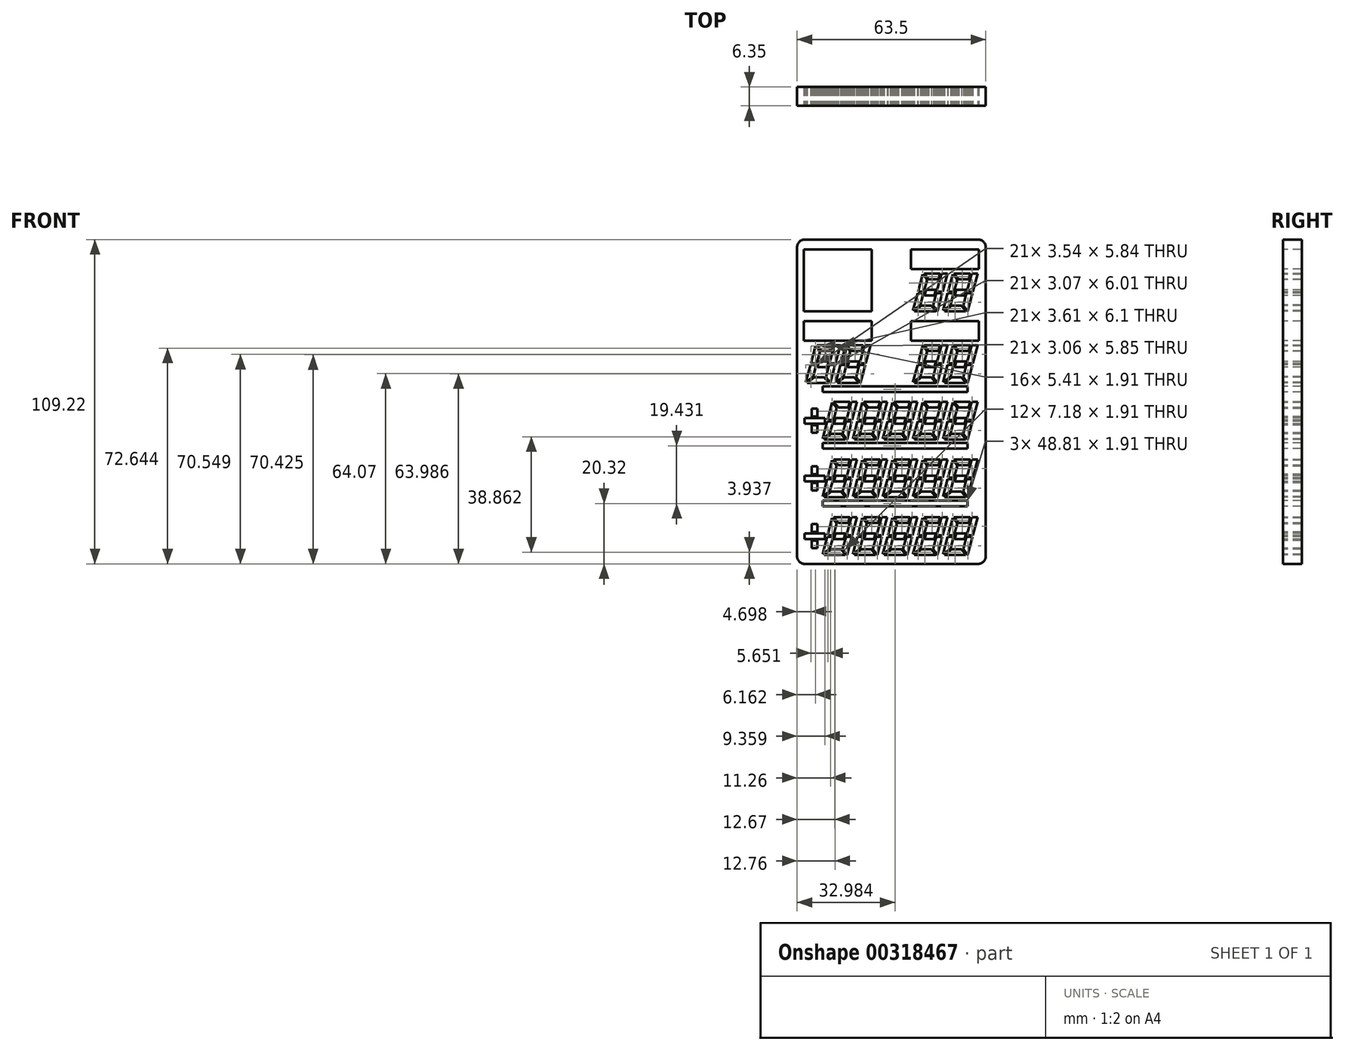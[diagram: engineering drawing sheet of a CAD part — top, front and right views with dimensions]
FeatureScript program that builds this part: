
annotation { "Feature Type Name" : "Feature", "Feature Type Description" : "" }
export const myFeature = defineFeature(function(context is Context, id is Id, definition is map)
    precondition{}
    {
        {
            var Q0;
            Q0=qCreatedBy(makeId("Front.planeOp"),FACE);
            var sketch = newSketch(context, id + "F0", { "sketchPlane" : qUnion([Q0])});
            skLineSegment(sketch, "E0.bottom", {"start": v(31.75, -54.61) * mm, "end": v(-31.75, -54.61) * mm});
            skLineSegment(sketch, "E0.top", {"start": v(31.75, 54.61) * mm, "end": v(-31.75, 54.6) * mm});
            skLineSegment(sketch, "E0.left", {"start": v(31.75, -54.61) * mm, "end": v(31.75, 54.61) * mm});
            skLineSegment(sketch, "E0.right", {"start": v(-31.75, -54.61) * mm, "end": v(-31.75, 54.6) * mm});
            skPoint(sketch, "E0.middle", {"position": v(0, 0) * mm});
            skSolve(sketch);
        }
        {
            var Q0;
            Q0 = qSketchRegion(id + "F0", true);
            extrude(context, id + "F1", {"entities" : qUnion([Q0]), "depth" : 6.35 * mm});
        }
        {
            var Q0;
            Q0=makeQuery(id+"F1.opExtrude","CAP_FACE",FACE,{"disambiguationData":[OSD([sQuery(id+"F0.wireOp",EDGE,"E0.bottom"),sQuery(id+"F0.wireOp",EDGE,"E0.top"),sQuery(id+"F0.wireOp",EDGE,"E0.left"),sQuery(id+"F0.wireOp",EDGE,"E0.right")])],"isStart":false});
            var sketch = newSketch(context, id + "F2", { "sketchPlane" : qUnion([Q0])});
            skLineSegment(sketch, "E1", {"start": v(21.11, -38.93) * mm, "end": v(26.52, -38.93) * mm});
            skLineSegment(sketch, "E2", {"start": v(26.52, -38.93) * mm, "end": v(26.01, -40.83) * mm});
            skLineSegment(sketch, "E3", {"start": v(26.01, -40.83) * mm, "end": v(22.7, -40.83) * mm});
            skLineSegment(sketch, "E4", {"start": v(22.7, -40.83) * mm, "end": v(21.11, -38.93) * mm});
            skLineSegment(sketch, "E5", {"start": v(27.05, -38.93) * mm, "end": v(29.02, -38.93) * mm});
            skLineSegment(sketch, "E6", {"start": v(29.02, -38.93) * mm, "end": v(27.39, -45.02) * mm});
            skLineSegment(sketch, "E7", {"start": v(27.05, -38.93) * mm, "end": v(25.41, -45.02) * mm});
            skLineSegment(sketch, "E8", {"start": v(25.41, -45.02) * mm, "end": v(27.39, -45.02) * mm});
            skLineSegment(sketch, "E9", {"start": v(25.28, -45.53) * mm, "end": v(27.25, -45.53) * mm});
            skLineSegment(sketch, "E10", {"start": v(27.25, -45.53) * mm, "end": v(25.64, -51.54) * mm});
            skLineSegment(sketch, "E11", {"start": v(20.65, -39.17) * mm, "end": v(22.15, -40.95) * mm});
            skLineSegment(sketch, "E12", {"start": v(22.15, -40.95) * mm, "end": v(21.06, -45.02) * mm});
            skLineSegment(sketch, "E13", {"start": v(21.06, -45.02) * mm, "end": v(19.09, -45.02) * mm});
            skLineSegment(sketch, "E14", {"start": v(19.09, -45.02) * mm, "end": v(20.65, -39.17) * mm});
            skLineSegment(sketch, "E15", {"start": v(25.28, -45.53) * mm, "end": v(24.18, -49.61) * mm});
            skLineSegment(sketch, "E16", {"start": v(24.18, -49.61) * mm, "end": v(25.64, -51.54) * mm});
            skLineSegment(sketch, "E17", {"start": v(25.06, -51.63) * mm, "end": v(23.63, -49.72) * mm});
            skLineSegment(sketch, "E18", {"start": v(23.63, -49.72) * mm, "end": v(20.33, -49.72) * mm});
            skLineSegment(sketch, "E19", {"start": v(25.06, -51.63) * mm, "end": v(17.89, -51.63) * mm});
            skLineSegment(sketch, "E20", {"start": v(17.89, -51.63) * mm, "end": v(20.33, -49.72) * mm});
            skLineSegment(sketch, "E21", {"start": v(20.92, -45.53) * mm, "end": v(18.95, -45.53) * mm});
            skLineSegment(sketch, "E22", {"start": v(18.95, -45.53) * mm, "end": v(17.39, -51.37) * mm});
            skLineSegment(sketch, "E23", {"start": v(17.39, -51.37) * mm, "end": v(19.88, -49.42) * mm});
            skLineSegment(sketch, "E24", {"start": v(19.88, -49.42) * mm, "end": v(20.92, -45.53) * mm});
            skLineSegment(sketch, "E25", {"start": v(21.77, -44.32) * mm, "end": v(21.26, -46.23) * mm});
            skLineSegment(sketch, "E26", {"start": v(21.26, -46.23) * mm, "end": v(24.56, -46.23) * mm});
            skLineSegment(sketch, "E27", {"start": v(24.56, -46.23) * mm, "end": v(25.08, -44.32) * mm});
            skLineSegment(sketch, "E28", {"start": v(25.08, -44.32) * mm, "end": v(21.77, -44.32) * mm});
            skLineSegment(sketch, "E29.0.1.0", {"start": v(21.26, -26.8) * mm, "end": v(24.56, -26.8) * mm});
            skLineSegment(sketch, "E29.0.1.1", {"start": v(18.95, -26.1) * mm, "end": v(17.39, -31.94) * mm});
            skLineSegment(sketch, "E29.0.1.2", {"start": v(22.15, -21.52) * mm, "end": v(21.06, -25.6) * mm});
            skLineSegment(sketch, "E29.0.1.3", {"start": v(29.02, -19.5) * mm, "end": v(27.39, -25.6) * mm});
            skLineSegment(sketch, "E29.0.1.4", {"start": v(26.01, -21.4) * mm, "end": v(22.7, -21.4) * mm});
            skLineSegment(sketch, "E29.0.1.5", {"start": v(25.06, -32.2) * mm, "end": v(17.89, -32.2) * mm});
            skLineSegment(sketch, "E29.0.1.6", {"start": v(27.05, -19.5) * mm, "end": v(25.41, -25.6) * mm});
            skLineSegment(sketch, "E29.0.1.7", {"start": v(23.63, -30.29) * mm, "end": v(20.33, -30.29) * mm});
            skLineSegment(sketch, "E29.0.1.8", {"start": v(25.08, -24.9) * mm, "end": v(21.77, -24.9) * mm});
            skLineSegment(sketch, "E29.0.1.9", {"start": v(25.28, -26.1) * mm, "end": v(24.18, -30.18) * mm});
            skLineSegment(sketch, "E29.0.1.10", {"start": v(27.25, -26.1) * mm, "end": v(25.64, -32.11) * mm});
            skLineSegment(sketch, "E29.0.1.11", {"start": v(19.09, -25.6) * mm, "end": v(20.65, -19.74) * mm});
            skLineSegment(sketch, "E29.0.1.12", {"start": v(21.11, -19.5) * mm, "end": v(26.52, -19.5) * mm});
            skLineSegment(sketch, "E29.0.1.13", {"start": v(20.65, -19.74) * mm, "end": v(22.15, -21.52) * mm});
            skLineSegment(sketch, "E29.0.1.14", {"start": v(21.06, -25.6) * mm, "end": v(19.09, -25.6) * mm});
            skLineSegment(sketch, "E29.0.1.15", {"start": v(19.88, -30) * mm, "end": v(20.92, -26.1) * mm});
            skLineSegment(sketch, "E29.0.1.16", {"start": v(22.7, -21.4) * mm, "end": v(21.11, -19.5) * mm});
            skLineSegment(sketch, "E29.0.1.17", {"start": v(17.89, -32.2) * mm, "end": v(20.33, -30.29) * mm});
            skLineSegment(sketch, "E29.0.1.18", {"start": v(27.05, -19.5) * mm, "end": v(29.02, -19.5) * mm});
            skLineSegment(sketch, "E29.0.1.19", {"start": v(20.92, -26.1) * mm, "end": v(18.95, -26.1) * mm});
            skLineSegment(sketch, "E29.0.1.20", {"start": v(17.39, -31.94) * mm, "end": v(19.88, -30) * mm});
            skLineSegment(sketch, "E29.0.1.21", {"start": v(25.06, -32.2) * mm, "end": v(23.63, -30.29) * mm});
            skLineSegment(sketch, "E29.0.1.22", {"start": v(26.52, -19.5) * mm, "end": v(26.01, -21.4) * mm});
            skLineSegment(sketch, "E29.0.1.23", {"start": v(24.18, -30.18) * mm, "end": v(25.64, -32.11) * mm});
            skLineSegment(sketch, "E29.0.1.24", {"start": v(21.77, -24.9) * mm, "end": v(21.26, -26.8) * mm});
            skLineSegment(sketch, "E29.0.1.25", {"start": v(25.28, -26.1) * mm, "end": v(27.25, -26.1) * mm});
            skLineSegment(sketch, "E29.0.1.26", {"start": v(25.41, -25.6) * mm, "end": v(27.39, -25.6) * mm});
            skLineSegment(sketch, "E29.0.1.27", {"start": v(24.56, -26.8) * mm, "end": v(25.08, -24.9) * mm});
            skLineSegment(sketch, "E29.0.2.0", {"start": v(21.26, -7.37) * mm, "end": v(24.56, -7.37) * mm});
            skLineSegment(sketch, "E29.0.2.1", {"start": v(18.95, -6.67) * mm, "end": v(17.39, -12.51) * mm});
            skLineSegment(sketch, "E29.0.2.2", {"start": v(22.15, -2.1) * mm, "end": v(21.06, -6.16) * mm});
            skLineSegment(sketch, "E29.0.2.3", {"start": v(29.02, -0.06) * mm, "end": v(27.39, -6.16) * mm});
            skLineSegment(sketch, "E29.0.2.4", {"start": v(26.01, -1.97) * mm, "end": v(22.7, -1.97) * mm});
            skLineSegment(sketch, "E29.0.2.5", {"start": v(25.06, -12.76) * mm, "end": v(17.89, -12.76) * mm});
            skLineSegment(sketch, "E29.0.2.6", {"start": v(27.05, -0.06) * mm, "end": v(25.41, -6.16) * mm});
            skLineSegment(sketch, "E29.0.2.7", {"start": v(23.63, -10.86) * mm, "end": v(20.33, -10.86) * mm});
            skLineSegment(sketch, "E29.0.2.8", {"start": v(25.08, -5.46) * mm, "end": v(21.77, -5.46) * mm});
            skLineSegment(sketch, "E29.0.2.9", {"start": v(25.28, -6.67) * mm, "end": v(24.18, -10.75) * mm});
            skLineSegment(sketch, "E29.0.2.10", {"start": v(27.25, -6.67) * mm, "end": v(25.64, -12.68) * mm});
            skLineSegment(sketch, "E29.0.2.11", {"start": v(19.09, -6.16) * mm, "end": v(20.65, -0.31) * mm});
            skLineSegment(sketch, "E29.0.2.12", {"start": v(21.11, -0.06) * mm, "end": v(26.52, -0.06) * mm});
            skLineSegment(sketch, "E29.0.2.13", {"start": v(20.65, -0.31) * mm, "end": v(22.15, -2.1) * mm});
            skLineSegment(sketch, "E29.0.2.14", {"start": v(21.06, -6.16) * mm, "end": v(19.09, -6.16) * mm});
            skLineSegment(sketch, "E29.0.2.15", {"start": v(19.88, -10.56) * mm, "end": v(20.92, -6.67) * mm});
            skLineSegment(sketch, "E29.0.2.16", {"start": v(22.7, -1.97) * mm, "end": v(21.11, -0.06) * mm});
            skLineSegment(sketch, "E29.0.2.17", {"start": v(17.89, -12.76) * mm, "end": v(20.33, -10.86) * mm});
            skLineSegment(sketch, "E29.0.2.18", {"start": v(27.05, -0.06) * mm, "end": v(29.02, -0.06) * mm});
            skLineSegment(sketch, "E29.0.2.19", {"start": v(20.92, -6.67) * mm, "end": v(18.95, -6.67) * mm});
            skLineSegment(sketch, "E29.0.2.20", {"start": v(17.39, -12.51) * mm, "end": v(19.88, -10.56) * mm});
            skLineSegment(sketch, "E29.0.2.21", {"start": v(25.06, -12.76) * mm, "end": v(23.63, -10.86) * mm});
            skLineSegment(sketch, "E29.0.2.22", {"start": v(26.52, -0.06) * mm, "end": v(26.01, -1.97) * mm});
            skLineSegment(sketch, "E29.0.2.23", {"start": v(24.18, -10.75) * mm, "end": v(25.64, -12.68) * mm});
            skLineSegment(sketch, "E29.0.2.24", {"start": v(21.77, -5.46) * mm, "end": v(21.26, -7.37) * mm});
            skLineSegment(sketch, "E29.0.2.25", {"start": v(25.28, -6.67) * mm, "end": v(27.25, -6.67) * mm});
            skLineSegment(sketch, "E29.0.2.26", {"start": v(25.41, -6.16) * mm, "end": v(27.39, -6.16) * mm});
            skLineSegment(sketch, "E29.0.2.27", {"start": v(24.56, -7.37) * mm, "end": v(25.08, -5.46) * mm});
            skLineSegment(sketch, "E29.1.0.0", {"start": v(11.12, -46.23) * mm, "end": v(14.43, -46.23) * mm});
            skLineSegment(sketch, "E29.1.0.1", {"start": v(8.81, -45.53) * mm, "end": v(7.25, -51.37) * mm});
            skLineSegment(sketch, "E29.1.0.2", {"start": v(12.01, -40.95) * mm, "end": v(10.92, -45.02) * mm});
            skLineSegment(sketch, "E29.1.0.3", {"start": v(18.88, -38.93) * mm, "end": v(17.25, -45.02) * mm});
            skLineSegment(sketch, "E29.1.0.4", {"start": v(15.87, -40.83) * mm, "end": v(12.57, -40.83) * mm});
            skLineSegment(sketch, "E29.1.0.5", {"start": v(14.93, -51.63) * mm, "end": v(7.75, -51.63) * mm});
            skLineSegment(sketch, "E29.1.0.6", {"start": v(16.9, -38.93) * mm, "end": v(15.27, -45.02) * mm});
            skLineSegment(sketch, "E29.1.0.7", {"start": v(13.49, -49.72) * mm, "end": v(10.19, -49.72) * mm});
            skLineSegment(sketch, "E29.1.0.8", {"start": v(14.94, -44.32) * mm, "end": v(11.63, -44.32) * mm});
            skLineSegment(sketch, "E29.1.0.9", {"start": v(15.14, -45.53) * mm, "end": v(14.04, -49.61) * mm});
            skLineSegment(sketch, "E29.1.0.10", {"start": v(17.11, -45.53) * mm, "end": v(15.5, -51.54) * mm});
            skLineSegment(sketch, "E29.1.0.11", {"start": v(8.95, -45.02) * mm, "end": v(10.52, -39.17) * mm});
            skLineSegment(sketch, "E29.1.0.12", {"start": v(10.97, -38.93) * mm, "end": v(16.38, -38.93) * mm});
            skLineSegment(sketch, "E29.1.0.13", {"start": v(10.52, -39.17) * mm, "end": v(12.01, -40.95) * mm});
            skLineSegment(sketch, "E29.1.0.14", {"start": v(10.92, -45.02) * mm, "end": v(8.95, -45.02) * mm});
            skLineSegment(sketch, "E29.1.0.15", {"start": v(9.74, -49.42) * mm, "end": v(10.78, -45.53) * mm});
            skLineSegment(sketch, "E29.1.0.16", {"start": v(12.57, -40.83) * mm, "end": v(10.97, -38.93) * mm});
            skLineSegment(sketch, "E29.1.0.17", {"start": v(7.75, -51.63) * mm, "end": v(10.19, -49.72) * mm});
            skLineSegment(sketch, "E29.1.0.18", {"start": v(16.9, -38.93) * mm, "end": v(18.88, -38.93) * mm});
            skLineSegment(sketch, "E29.1.0.19", {"start": v(10.78, -45.53) * mm, "end": v(8.81, -45.53) * mm});
            skLineSegment(sketch, "E29.1.0.20", {"start": v(7.25, -51.37) * mm, "end": v(9.74, -49.42) * mm});
            skLineSegment(sketch, "E29.1.0.21", {"start": v(14.93, -51.63) * mm, "end": v(13.49, -49.72) * mm});
            skLineSegment(sketch, "E29.1.0.22", {"start": v(16.38, -38.93) * mm, "end": v(15.87, -40.83) * mm});
            skLineSegment(sketch, "E29.1.0.23", {"start": v(14.04, -49.61) * mm, "end": v(15.5, -51.54) * mm});
            skLineSegment(sketch, "E29.1.0.24", {"start": v(11.63, -44.32) * mm, "end": v(11.12, -46.23) * mm});
            skLineSegment(sketch, "E29.1.0.25", {"start": v(15.14, -45.53) * mm, "end": v(17.11, -45.53) * mm});
            skLineSegment(sketch, "E29.1.0.26", {"start": v(15.27, -45.02) * mm, "end": v(17.25, -45.02) * mm});
            skLineSegment(sketch, "E29.1.0.27", {"start": v(14.43, -46.23) * mm, "end": v(14.94, -44.32) * mm});
            skLineSegment(sketch, "E29.1.1.0", {"start": v(11.12, -26.8) * mm, "end": v(14.43, -26.8) * mm});
            skLineSegment(sketch, "E29.1.1.1", {"start": v(8.81, -26.1) * mm, "end": v(7.25, -31.94) * mm});
            skLineSegment(sketch, "E29.1.1.2", {"start": v(12.01, -21.52) * mm, "end": v(10.92, -25.6) * mm});
            skLineSegment(sketch, "E29.1.1.3", {"start": v(18.88, -19.5) * mm, "end": v(17.25, -25.6) * mm});
            skLineSegment(sketch, "E29.1.1.4", {"start": v(15.87, -21.4) * mm, "end": v(12.57, -21.4) * mm});
            skLineSegment(sketch, "E29.1.1.5", {"start": v(14.93, -32.2) * mm, "end": v(7.75, -32.2) * mm});
            skLineSegment(sketch, "E29.1.1.6", {"start": v(16.9, -19.5) * mm, "end": v(15.27, -25.6) * mm});
            skLineSegment(sketch, "E29.1.1.7", {"start": v(13.49, -30.29) * mm, "end": v(10.19, -30.29) * mm});
            skLineSegment(sketch, "E29.1.1.8", {"start": v(14.94, -24.9) * mm, "end": v(11.63, -24.9) * mm});
            skLineSegment(sketch, "E29.1.1.9", {"start": v(15.14, -26.1) * mm, "end": v(14.04, -30.18) * mm});
            skLineSegment(sketch, "E29.1.1.10", {"start": v(17.11, -26.1) * mm, "end": v(15.5, -32.11) * mm});
            skLineSegment(sketch, "E29.1.1.11", {"start": v(8.95, -25.6) * mm, "end": v(10.52, -19.74) * mm});
            skLineSegment(sketch, "E29.1.1.12", {"start": v(10.97, -19.5) * mm, "end": v(16.38, -19.5) * mm});
            skLineSegment(sketch, "E29.1.1.13", {"start": v(10.52, -19.74) * mm, "end": v(12.01, -21.52) * mm});
            skLineSegment(sketch, "E29.1.1.14", {"start": v(10.92, -25.6) * mm, "end": v(8.95, -25.6) * mm});
            skLineSegment(sketch, "E29.1.1.15", {"start": v(9.74, -30) * mm, "end": v(10.78, -26.1) * mm});
            skLineSegment(sketch, "E29.1.1.16", {"start": v(12.57, -21.4) * mm, "end": v(10.97, -19.5) * mm});
            skLineSegment(sketch, "E29.1.1.17", {"start": v(7.75, -32.2) * mm, "end": v(10.19, -30.29) * mm});
            skLineSegment(sketch, "E29.1.1.18", {"start": v(16.9, -19.5) * mm, "end": v(18.88, -19.5) * mm});
            skLineSegment(sketch, "E29.1.1.19", {"start": v(10.78, -26.1) * mm, "end": v(8.81, -26.1) * mm});
            skLineSegment(sketch, "E29.1.1.20", {"start": v(7.25, -31.94) * mm, "end": v(9.74, -30) * mm});
            skLineSegment(sketch, "E29.1.1.21", {"start": v(14.93, -32.2) * mm, "end": v(13.49, -30.29) * mm});
            skLineSegment(sketch, "E29.1.1.22", {"start": v(16.38, -19.5) * mm, "end": v(15.87, -21.4) * mm});
            skLineSegment(sketch, "E29.1.1.23", {"start": v(14.04, -30.18) * mm, "end": v(15.5, -32.11) * mm});
            skLineSegment(sketch, "E29.1.1.24", {"start": v(11.63, -24.9) * mm, "end": v(11.12, -26.8) * mm});
            skLineSegment(sketch, "E29.1.1.25", {"start": v(15.14, -26.1) * mm, "end": v(17.11, -26.1) * mm});
            skLineSegment(sketch, "E29.1.1.26", {"start": v(15.27, -25.6) * mm, "end": v(17.25, -25.6) * mm});
            skLineSegment(sketch, "E29.1.1.27", {"start": v(14.43, -26.8) * mm, "end": v(14.94, -24.9) * mm});
            skLineSegment(sketch, "E29.1.2.0", {"start": v(11.12, -7.37) * mm, "end": v(14.43, -7.37) * mm});
            skLineSegment(sketch, "E29.1.2.1", {"start": v(8.81, -6.67) * mm, "end": v(7.25, -12.51) * mm});
            skLineSegment(sketch, "E29.1.2.2", {"start": v(12.01, -2.1) * mm, "end": v(10.92, -6.16) * mm});
            skLineSegment(sketch, "E29.1.2.3", {"start": v(18.88, -0.06) * mm, "end": v(17.25, -6.16) * mm});
            skLineSegment(sketch, "E29.1.2.4", {"start": v(15.87, -1.97) * mm, "end": v(12.57, -1.97) * mm});
            skLineSegment(sketch, "E29.1.2.5", {"start": v(14.93, -12.76) * mm, "end": v(7.75, -12.76) * mm});
            skLineSegment(sketch, "E29.1.2.6", {"start": v(16.9, -0.06) * mm, "end": v(15.27, -6.16) * mm});
            skLineSegment(sketch, "E29.1.2.7", {"start": v(13.49, -10.86) * mm, "end": v(10.19, -10.86) * mm});
            skLineSegment(sketch, "E29.1.2.8", {"start": v(14.94, -5.46) * mm, "end": v(11.63, -5.46) * mm});
            skLineSegment(sketch, "E29.1.2.9", {"start": v(15.14, -6.67) * mm, "end": v(14.04, -10.75) * mm});
            skLineSegment(sketch, "E29.1.2.10", {"start": v(17.11, -6.67) * mm, "end": v(15.5, -12.68) * mm});
            skLineSegment(sketch, "E29.1.2.11", {"start": v(8.95, -6.16) * mm, "end": v(10.52, -0.31) * mm});
            skLineSegment(sketch, "E29.1.2.12", {"start": v(10.97, -0.06) * mm, "end": v(16.38, -0.06) * mm});
            skLineSegment(sketch, "E29.1.2.13", {"start": v(10.52, -0.31) * mm, "end": v(12.01, -2.1) * mm});
            skLineSegment(sketch, "E29.1.2.14", {"start": v(10.92, -6.16) * mm, "end": v(8.95, -6.16) * mm});
            skLineSegment(sketch, "E29.1.2.15", {"start": v(9.74, -10.56) * mm, "end": v(10.78, -6.67) * mm});
            skLineSegment(sketch, "E29.1.2.16", {"start": v(12.57, -1.97) * mm, "end": v(10.97, -0.06) * mm});
            skLineSegment(sketch, "E29.1.2.17", {"start": v(7.75, -12.76) * mm, "end": v(10.19, -10.86) * mm});
            skLineSegment(sketch, "E29.1.2.18", {"start": v(16.9, -0.06) * mm, "end": v(18.88, -0.06) * mm});
            skLineSegment(sketch, "E29.1.2.19", {"start": v(10.78, -6.67) * mm, "end": v(8.81, -6.67) * mm});
            skLineSegment(sketch, "E29.1.2.20", {"start": v(7.25, -12.51) * mm, "end": v(9.74, -10.56) * mm});
            skLineSegment(sketch, "E29.1.2.21", {"start": v(14.93, -12.76) * mm, "end": v(13.49, -10.86) * mm});
            skLineSegment(sketch, "E29.1.2.22", {"start": v(16.38, -0.06) * mm, "end": v(15.87, -1.97) * mm});
            skLineSegment(sketch, "E29.1.2.23", {"start": v(14.04, -10.75) * mm, "end": v(15.5, -12.68) * mm});
            skLineSegment(sketch, "E29.1.2.24", {"start": v(11.63, -5.46) * mm, "end": v(11.12, -7.37) * mm});
            skLineSegment(sketch, "E29.1.2.25", {"start": v(15.14, -6.67) * mm, "end": v(17.11, -6.67) * mm});
            skLineSegment(sketch, "E29.1.2.26", {"start": v(15.27, -6.16) * mm, "end": v(17.25, -6.16) * mm});
            skLineSegment(sketch, "E29.1.2.27", {"start": v(14.43, -7.37) * mm, "end": v(14.94, -5.46) * mm});
            skLineSegment(sketch, "E29.2.0.0", {"start": v(0.98, -46.23) * mm, "end": v(4.29, -46.23) * mm});
            skLineSegment(sketch, "E29.2.0.1", {"start": v(-1.33, -45.53) * mm, "end": v(-2.9, -51.37) * mm});
            skLineSegment(sketch, "E29.2.0.2", {"start": v(1.87, -40.95) * mm, "end": v(0.78, -45.02) * mm});
            skLineSegment(sketch, "E29.2.0.3", {"start": v(8.74, -38.93) * mm, "end": v(7.1, -45.02) * mm});
            skLineSegment(sketch, "E29.2.0.4", {"start": v(5.73, -40.83) * mm, "end": v(2.43, -40.83) * mm});
            skLineSegment(sketch, "E29.2.0.5", {"start": v(4.79, -51.63) * mm, "end": v(-2.39, -51.63) * mm});
            skLineSegment(sketch, "E29.2.0.6", {"start": v(6.77, -38.93) * mm, "end": v(5.14, -45.02) * mm});
            skLineSegment(sketch, "E29.2.0.7", {"start": v(3.35, -49.72) * mm, "end": v(0.05, -49.72) * mm});
            skLineSegment(sketch, "E29.2.0.8", {"start": v(4.8, -44.32) * mm, "end": v(1.5, -44.32) * mm});
            skLineSegment(sketch, "E29.2.0.9", {"start": v(5, -45.53) * mm, "end": v(3.9, -49.61) * mm});
            skLineSegment(sketch, "E29.2.0.10", {"start": v(6.97, -45.53) * mm, "end": v(5.36, -51.54) * mm});
            skLineSegment(sketch, "E29.2.0.11", {"start": v(-1.2, -45.02) * mm, "end": v(0.38, -39.17) * mm});
            skLineSegment(sketch, "E29.2.0.12", {"start": v(0.83, -38.93) * mm, "end": v(6.24, -38.93) * mm});
            skLineSegment(sketch, "E29.2.0.13", {"start": v(0.38, -39.17) * mm, "end": v(1.87, -40.95) * mm});
            skLineSegment(sketch, "E29.2.0.14", {"start": v(0.78, -45.02) * mm, "end": v(-1.2, -45.02) * mm});
            skLineSegment(sketch, "E29.2.0.15", {"start": v(-0.4, -49.42) * mm, "end": v(0.65, -45.53) * mm});
            skLineSegment(sketch, "E29.2.0.16", {"start": v(2.43, -40.83) * mm, "end": v(0.83, -38.93) * mm});
            skLineSegment(sketch, "E29.2.0.17", {"start": v(-2.39, -51.63) * mm, "end": v(0.05, -49.72) * mm});
            skLineSegment(sketch, "E29.2.0.18", {"start": v(6.77, -38.93) * mm, "end": v(8.74, -38.93) * mm});
            skLineSegment(sketch, "E29.2.0.19", {"start": v(0.65, -45.53) * mm, "end": v(-1.33, -45.53) * mm});
            skLineSegment(sketch, "E29.2.0.20", {"start": v(-2.9, -51.37) * mm, "end": v(-0.4, -49.42) * mm});
            skLineSegment(sketch, "E29.2.0.21", {"start": v(4.79, -51.63) * mm, "end": v(3.35, -49.72) * mm});
            skLineSegment(sketch, "E29.2.0.22", {"start": v(6.24, -38.93) * mm, "end": v(5.73, -40.83) * mm});
            skLineSegment(sketch, "E29.2.0.23", {"start": v(3.9, -49.61) * mm, "end": v(5.36, -51.54) * mm});
            skLineSegment(sketch, "E29.2.0.24", {"start": v(1.5, -44.32) * mm, "end": v(0.98, -46.23) * mm});
            skLineSegment(sketch, "E29.2.0.25", {"start": v(5, -45.53) * mm, "end": v(6.97, -45.53) * mm});
            skLineSegment(sketch, "E29.2.0.26", {"start": v(5.14, -45.02) * mm, "end": v(7.1, -45.02) * mm});
            skLineSegment(sketch, "E29.2.0.27", {"start": v(4.29, -46.23) * mm, "end": v(4.8, -44.32) * mm});
            skLineSegment(sketch, "E29.2.1.0", {"start": v(0.98, -26.8) * mm, "end": v(4.29, -26.8) * mm});
            skLineSegment(sketch, "E29.2.1.1", {"start": v(-1.33, -26.1) * mm, "end": v(-2.9, -31.94) * mm});
            skLineSegment(sketch, "E29.2.1.2", {"start": v(1.87, -21.52) * mm, "end": v(0.78, -25.6) * mm});
            skLineSegment(sketch, "E29.2.1.3", {"start": v(8.74, -19.5) * mm, "end": v(7.1, -25.6) * mm});
            skLineSegment(sketch, "E29.2.1.4", {"start": v(5.73, -21.4) * mm, "end": v(2.43, -21.4) * mm});
            skLineSegment(sketch, "E29.2.1.5", {"start": v(4.79, -32.2) * mm, "end": v(-2.39, -32.2) * mm});
            skLineSegment(sketch, "E29.2.1.6", {"start": v(6.77, -19.5) * mm, "end": v(5.14, -25.6) * mm});
            skLineSegment(sketch, "E29.2.1.7", {"start": v(3.35, -30.29) * mm, "end": v(0.05, -30.29) * mm});
            skLineSegment(sketch, "E29.2.1.8", {"start": v(4.8, -24.9) * mm, "end": v(1.5, -24.9) * mm});
            skLineSegment(sketch, "E29.2.1.9", {"start": v(5, -26.1) * mm, "end": v(3.9, -30.18) * mm});
            skLineSegment(sketch, "E29.2.1.10", {"start": v(6.97, -26.1) * mm, "end": v(5.36, -32.11) * mm});
            skLineSegment(sketch, "E29.2.1.11", {"start": v(-1.2, -25.6) * mm, "end": v(0.38, -19.74) * mm});
            skLineSegment(sketch, "E29.2.1.12", {"start": v(0.83, -19.5) * mm, "end": v(6.24, -19.5) * mm});
            skLineSegment(sketch, "E29.2.1.13", {"start": v(0.38, -19.74) * mm, "end": v(1.87, -21.52) * mm});
            skLineSegment(sketch, "E29.2.1.14", {"start": v(0.78, -25.6) * mm, "end": v(-1.2, -25.6) * mm});
            skLineSegment(sketch, "E29.2.1.15", {"start": v(-0.4, -30) * mm, "end": v(0.65, -26.1) * mm});
            skLineSegment(sketch, "E29.2.1.16", {"start": v(2.43, -21.4) * mm, "end": v(0.83, -19.5) * mm});
            skLineSegment(sketch, "E29.2.1.17", {"start": v(-2.39, -32.2) * mm, "end": v(0.05, -30.29) * mm});
            skLineSegment(sketch, "E29.2.1.18", {"start": v(6.77, -19.5) * mm, "end": v(8.74, -19.5) * mm});
            skLineSegment(sketch, "E29.2.1.19", {"start": v(0.65, -26.1) * mm, "end": v(-1.33, -26.1) * mm});
            skLineSegment(sketch, "E29.2.1.20", {"start": v(-2.9, -31.94) * mm, "end": v(-0.4, -30) * mm});
            skLineSegment(sketch, "E29.2.1.21", {"start": v(4.79, -32.2) * mm, "end": v(3.35, -30.29) * mm});
            skLineSegment(sketch, "E29.2.1.22", {"start": v(6.24, -19.5) * mm, "end": v(5.73, -21.4) * mm});
            skLineSegment(sketch, "E29.2.1.23", {"start": v(3.9, -30.18) * mm, "end": v(5.36, -32.11) * mm});
            skLineSegment(sketch, "E29.2.1.24", {"start": v(1.5, -24.9) * mm, "end": v(0.98, -26.8) * mm});
            skLineSegment(sketch, "E29.2.1.25", {"start": v(5, -26.1) * mm, "end": v(6.97, -26.1) * mm});
            skLineSegment(sketch, "E29.2.1.26", {"start": v(5.14, -25.6) * mm, "end": v(7.1, -25.6) * mm});
            skLineSegment(sketch, "E29.2.1.27", {"start": v(4.29, -26.8) * mm, "end": v(4.8, -24.9) * mm});
            skLineSegment(sketch, "E29.2.2.0", {"start": v(0.98, -7.37) * mm, "end": v(4.29, -7.37) * mm});
            skLineSegment(sketch, "E29.2.2.1", {"start": v(-1.33, -6.67) * mm, "end": v(-2.9, -12.51) * mm});
            skLineSegment(sketch, "E29.2.2.2", {"start": v(1.87, -2.1) * mm, "end": v(0.78, -6.16) * mm});
            skLineSegment(sketch, "E29.2.2.3", {"start": v(8.74, -0.06) * mm, "end": v(7.1, -6.16) * mm});
            skLineSegment(sketch, "E29.2.2.4", {"start": v(5.73, -1.97) * mm, "end": v(2.43, -1.97) * mm});
            skLineSegment(sketch, "E29.2.2.5", {"start": v(4.79, -12.76) * mm, "end": v(-2.39, -12.76) * mm});
            skLineSegment(sketch, "E29.2.2.6", {"start": v(6.77, -0.06) * mm, "end": v(5.14, -6.16) * mm});
            skLineSegment(sketch, "E29.2.2.7", {"start": v(3.35, -10.86) * mm, "end": v(0.05, -10.86) * mm});
            skLineSegment(sketch, "E29.2.2.8", {"start": v(4.8, -5.46) * mm, "end": v(1.5, -5.46) * mm});
            skLineSegment(sketch, "E29.2.2.9", {"start": v(5, -6.67) * mm, "end": v(3.9, -10.75) * mm});
            skLineSegment(sketch, "E29.2.2.10", {"start": v(6.97, -6.67) * mm, "end": v(5.36, -12.68) * mm});
            skLineSegment(sketch, "E29.2.2.11", {"start": v(-1.2, -6.16) * mm, "end": v(0.38, -0.31) * mm});
            skLineSegment(sketch, "E29.2.2.12", {"start": v(0.83, -0.06) * mm, "end": v(6.24, -0.06) * mm});
            skLineSegment(sketch, "E29.2.2.13", {"start": v(0.38, -0.31) * mm, "end": v(1.87, -2.1) * mm});
            skLineSegment(sketch, "E29.2.2.14", {"start": v(0.78, -6.16) * mm, "end": v(-1.2, -6.16) * mm});
            skLineSegment(sketch, "E29.2.2.15", {"start": v(-0.4, -10.56) * mm, "end": v(0.65, -6.67) * mm});
            skLineSegment(sketch, "E29.2.2.16", {"start": v(2.43, -1.97) * mm, "end": v(0.83, -0.06) * mm});
            skLineSegment(sketch, "E29.2.2.17", {"start": v(-2.39, -12.76) * mm, "end": v(0.05, -10.86) * mm});
            skLineSegment(sketch, "E29.2.2.18", {"start": v(6.77, -0.06) * mm, "end": v(8.74, -0.06) * mm});
            skLineSegment(sketch, "E29.2.2.19", {"start": v(0.65, -6.67) * mm, "end": v(-1.33, -6.67) * mm});
            skLineSegment(sketch, "E29.2.2.20", {"start": v(-2.9, -12.51) * mm, "end": v(-0.4, -10.56) * mm});
            skLineSegment(sketch, "E29.2.2.21", {"start": v(4.79, -12.76) * mm, "end": v(3.35, -10.86) * mm});
            skLineSegment(sketch, "E29.2.2.22", {"start": v(6.24, -0.06) * mm, "end": v(5.73, -1.97) * mm});
            skLineSegment(sketch, "E29.2.2.23", {"start": v(3.9, -10.75) * mm, "end": v(5.36, -12.68) * mm});
            skLineSegment(sketch, "E29.2.2.24", {"start": v(1.5, -5.46) * mm, "end": v(0.98, -7.37) * mm});
            skLineSegment(sketch, "E29.2.2.25", {"start": v(5, -6.67) * mm, "end": v(6.97, -6.67) * mm});
            skLineSegment(sketch, "E29.2.2.26", {"start": v(5.14, -6.16) * mm, "end": v(7.1, -6.16) * mm});
            skLineSegment(sketch, "E29.2.2.27", {"start": v(4.29, -7.37) * mm, "end": v(4.8, -5.46) * mm});
            skLineSegment(sketch, "E29.3.0.0", {"start": v(-9.15, -46.23) * mm, "end": v(-5.85, -46.23) * mm});
            skLineSegment(sketch, "E29.3.0.1", {"start": v(-11.47, -45.53) * mm, "end": v(-13.03, -51.37) * mm});
            skLineSegment(sketch, "E29.3.0.2", {"start": v(-8.27, -40.95) * mm, "end": v(-9.36, -45.02) * mm});
            skLineSegment(sketch, "E29.3.0.3", {"start": v(-1.4, -38.93) * mm, "end": v(-3.03, -45.02) * mm});
            skLineSegment(sketch, "E29.3.0.4", {"start": v(-4.4, -40.83) * mm, "end": v(-7.7, -40.83) * mm});
            skLineSegment(sketch, "E29.3.0.5", {"start": v(-5.35, -51.63) * mm, "end": v(-12.53, -51.63) * mm});
            skLineSegment(sketch, "E29.3.0.6", {"start": v(-3.37, -38.93) * mm, "end": v(-5, -45.02) * mm});
            skLineSegment(sketch, "E29.3.0.7", {"start": v(-6.79, -49.72) * mm, "end": v(-10.1, -49.72) * mm});
            skLineSegment(sketch, "E29.3.0.8", {"start": v(-5.34, -44.32) * mm, "end": v(-8.64, -44.32) * mm});
            skLineSegment(sketch, "E29.3.0.9", {"start": v(-5.14, -45.53) * mm, "end": v(-6.23, -49.61) * mm});
            skLineSegment(sketch, "E29.3.0.10", {"start": v(-3.17, -45.53) * mm, "end": v(-4.78, -51.54) * mm});
            skLineSegment(sketch, "E29.3.0.11", {"start": v(-11.33, -45.02) * mm, "end": v(-9.76, -39.17) * mm});
            skLineSegment(sketch, "E29.3.0.12", {"start": v(-9.3, -38.93) * mm, "end": v(-3.9, -38.93) * mm});
            skLineSegment(sketch, "E29.3.0.13", {"start": v(-9.76, -39.17) * mm, "end": v(-8.27, -40.95) * mm});
            skLineSegment(sketch, "E29.3.0.14", {"start": v(-9.36, -45.02) * mm, "end": v(-11.33, -45.02) * mm});
            skLineSegment(sketch, "E29.3.0.15", {"start": v(-10.54, -49.42) * mm, "end": v(-9.5, -45.53) * mm});
            skLineSegment(sketch, "E29.3.0.16", {"start": v(-7.7, -40.83) * mm, "end": v(-9.3, -38.93) * mm});
            skLineSegment(sketch, "E29.3.0.17", {"start": v(-12.53, -51.63) * mm, "end": v(-10.1, -49.72) * mm});
            skLineSegment(sketch, "E29.3.0.18", {"start": v(-3.37, -38.93) * mm, "end": v(-1.4, -38.93) * mm});
            skLineSegment(sketch, "E29.3.0.19", {"start": v(-9.5, -45.53) * mm, "end": v(-11.47, -45.53) * mm});
            skLineSegment(sketch, "E29.3.0.20", {"start": v(-13.03, -51.37) * mm, "end": v(-10.54, -49.42) * mm});
            skLineSegment(sketch, "E29.3.0.21", {"start": v(-5.35, -51.63) * mm, "end": v(-6.79, -49.72) * mm});
            skLineSegment(sketch, "E29.3.0.22", {"start": v(-3.9, -38.93) * mm, "end": v(-4.4, -40.83) * mm});
            skLineSegment(sketch, "E29.3.0.23", {"start": v(-6.23, -49.61) * mm, "end": v(-4.78, -51.54) * mm});
            skLineSegment(sketch, "E29.3.0.24", {"start": v(-8.64, -44.32) * mm, "end": v(-9.15, -46.23) * mm});
            skLineSegment(sketch, "E29.3.0.25", {"start": v(-5.14, -45.53) * mm, "end": v(-3.17, -45.53) * mm});
            skLineSegment(sketch, "E29.3.0.26", {"start": v(-5, -45.02) * mm, "end": v(-3.03, -45.02) * mm});
            skLineSegment(sketch, "E29.3.0.27", {"start": v(-5.85, -46.23) * mm, "end": v(-5.34, -44.32) * mm});
            skLineSegment(sketch, "E29.3.1.0", {"start": v(-9.15, -26.8) * mm, "end": v(-5.85, -26.8) * mm});
            skLineSegment(sketch, "E29.3.1.1", {"start": v(-11.47, -26.1) * mm, "end": v(-13.03, -31.94) * mm});
            skLineSegment(sketch, "E29.3.1.2", {"start": v(-8.27, -21.52) * mm, "end": v(-9.36, -25.6) * mm});
            skLineSegment(sketch, "E29.3.1.3", {"start": v(-1.4, -19.5) * mm, "end": v(-3.03, -25.6) * mm});
            skLineSegment(sketch, "E29.3.1.4", {"start": v(-4.4, -21.4) * mm, "end": v(-7.7, -21.4) * mm});
            skLineSegment(sketch, "E29.3.1.5", {"start": v(-5.35, -32.2) * mm, "end": v(-12.53, -32.2) * mm});
            skLineSegment(sketch, "E29.3.1.6", {"start": v(-3.37, -19.5) * mm, "end": v(-5, -25.6) * mm});
            skLineSegment(sketch, "E29.3.1.7", {"start": v(-6.79, -30.29) * mm, "end": v(-10.1, -30.29) * mm});
            skLineSegment(sketch, "E29.3.1.8", {"start": v(-5.34, -24.9) * mm, "end": v(-8.64, -24.9) * mm});
            skLineSegment(sketch, "E29.3.1.9", {"start": v(-5.14, -26.1) * mm, "end": v(-6.23, -30.18) * mm});
            skLineSegment(sketch, "E29.3.1.10", {"start": v(-3.17, -26.1) * mm, "end": v(-4.78, -32.11) * mm});
            skLineSegment(sketch, "E29.3.1.11", {"start": v(-11.33, -25.6) * mm, "end": v(-9.76, -19.74) * mm});
            skLineSegment(sketch, "E29.3.1.12", {"start": v(-9.3, -19.5) * mm, "end": v(-3.9, -19.5) * mm});
            skLineSegment(sketch, "E29.3.1.13", {"start": v(-9.76, -19.74) * mm, "end": v(-8.27, -21.52) * mm});
            skLineSegment(sketch, "E29.3.1.14", {"start": v(-9.36, -25.6) * mm, "end": v(-11.33, -25.6) * mm});
            skLineSegment(sketch, "E29.3.1.15", {"start": v(-10.54, -30) * mm, "end": v(-9.5, -26.1) * mm});
            skLineSegment(sketch, "E29.3.1.16", {"start": v(-7.7, -21.4) * mm, "end": v(-9.3, -19.5) * mm});
            skLineSegment(sketch, "E29.3.1.17", {"start": v(-12.53, -32.2) * mm, "end": v(-10.1, -30.29) * mm});
            skLineSegment(sketch, "E29.3.1.18", {"start": v(-3.37, -19.5) * mm, "end": v(-1.4, -19.5) * mm});
            skLineSegment(sketch, "E29.3.1.19", {"start": v(-9.5, -26.1) * mm, "end": v(-11.47, -26.1) * mm});
            skLineSegment(sketch, "E29.3.1.20", {"start": v(-13.03, -31.94) * mm, "end": v(-10.54, -30) * mm});
            skLineSegment(sketch, "E29.3.1.21", {"start": v(-5.35, -32.2) * mm, "end": v(-6.79, -30.29) * mm});
            skLineSegment(sketch, "E29.3.1.22", {"start": v(-3.9, -19.5) * mm, "end": v(-4.4, -21.4) * mm});
            skLineSegment(sketch, "E29.3.1.23", {"start": v(-6.23, -30.18) * mm, "end": v(-4.78, -32.11) * mm});
            skLineSegment(sketch, "E29.3.1.24", {"start": v(-8.64, -24.9) * mm, "end": v(-9.15, -26.8) * mm});
            skLineSegment(sketch, "E29.3.1.25", {"start": v(-5.14, -26.1) * mm, "end": v(-3.17, -26.1) * mm});
            skLineSegment(sketch, "E29.3.1.26", {"start": v(-5, -25.6) * mm, "end": v(-3.03, -25.6) * mm});
            skLineSegment(sketch, "E29.3.1.27", {"start": v(-5.85, -26.8) * mm, "end": v(-5.34, -24.9) * mm});
            skLineSegment(sketch, "E29.3.2.0", {"start": v(-9.15, -7.37) * mm, "end": v(-5.85, -7.37) * mm});
            skLineSegment(sketch, "E29.3.2.1", {"start": v(-11.47, -6.67) * mm, "end": v(-13.03, -12.51) * mm});
            skLineSegment(sketch, "E29.3.2.2", {"start": v(-8.27, -2.1) * mm, "end": v(-9.36, -6.16) * mm});
            skLineSegment(sketch, "E29.3.2.3", {"start": v(-1.4, -0.06) * mm, "end": v(-3.03, -6.16) * mm});
            skLineSegment(sketch, "E29.3.2.4", {"start": v(-4.4, -1.97) * mm, "end": v(-7.7, -1.97) * mm});
            skLineSegment(sketch, "E29.3.2.5", {"start": v(-5.35, -12.76) * mm, "end": v(-12.53, -12.76) * mm});
            skLineSegment(sketch, "E29.3.2.6", {"start": v(-3.37, -0.06) * mm, "end": v(-5, -6.16) * mm});
            skLineSegment(sketch, "E29.3.2.7", {"start": v(-6.79, -10.86) * mm, "end": v(-10.1, -10.86) * mm});
            skLineSegment(sketch, "E29.3.2.8", {"start": v(-5.34, -5.46) * mm, "end": v(-8.64, -5.46) * mm});
            skLineSegment(sketch, "E29.3.2.9", {"start": v(-5.14, -6.67) * mm, "end": v(-6.23, -10.75) * mm});
            skLineSegment(sketch, "E29.3.2.10", {"start": v(-3.17, -6.67) * mm, "end": v(-4.78, -12.68) * mm});
            skLineSegment(sketch, "E29.3.2.11", {"start": v(-11.33, -6.16) * mm, "end": v(-9.76, -0.31) * mm});
            skLineSegment(sketch, "E29.3.2.12", {"start": v(-9.3, -0.06) * mm, "end": v(-3.9, -0.06) * mm});
            skLineSegment(sketch, "E29.3.2.13", {"start": v(-9.76, -0.31) * mm, "end": v(-8.27, -2.1) * mm});
            skLineSegment(sketch, "E29.3.2.14", {"start": v(-9.36, -6.16) * mm, "end": v(-11.33, -6.16) * mm});
            skLineSegment(sketch, "E29.3.2.15", {"start": v(-10.54, -10.56) * mm, "end": v(-9.5, -6.67) * mm});
            skLineSegment(sketch, "E29.3.2.16", {"start": v(-7.7, -1.97) * mm, "end": v(-9.3, -0.06) * mm});
            skLineSegment(sketch, "E29.3.2.17", {"start": v(-12.53, -12.76) * mm, "end": v(-10.1, -10.86) * mm});
            skLineSegment(sketch, "E29.3.2.18", {"start": v(-3.37, -0.06) * mm, "end": v(-1.4, -0.06) * mm});
            skLineSegment(sketch, "E29.3.2.19", {"start": v(-9.5, -6.67) * mm, "end": v(-11.47, -6.67) * mm});
            skLineSegment(sketch, "E29.3.2.20", {"start": v(-13.03, -12.51) * mm, "end": v(-10.54, -10.56) * mm});
            skLineSegment(sketch, "E29.3.2.21", {"start": v(-5.35, -12.76) * mm, "end": v(-6.79, -10.86) * mm});
            skLineSegment(sketch, "E29.3.2.22", {"start": v(-3.9, -0.06) * mm, "end": v(-4.4, -1.97) * mm});
            skLineSegment(sketch, "E29.3.2.23", {"start": v(-6.23, -10.75) * mm, "end": v(-4.78, -12.68) * mm});
            skLineSegment(sketch, "E29.3.2.24", {"start": v(-8.64, -5.46) * mm, "end": v(-9.15, -7.37) * mm});
            skLineSegment(sketch, "E29.3.2.25", {"start": v(-5.14, -6.67) * mm, "end": v(-3.17, -6.67) * mm});
            skLineSegment(sketch, "E29.3.2.26", {"start": v(-5, -6.16) * mm, "end": v(-3.03, -6.16) * mm});
            skLineSegment(sketch, "E29.3.2.27", {"start": v(-5.85, -7.37) * mm, "end": v(-5.34, -5.46) * mm});
            skLineSegment(sketch, "E29.4.0.0", {"start": v(-19.3, -46.23) * mm, "end": v(-16, -46.23) * mm});
            skLineSegment(sketch, "E29.4.0.1", {"start": v(-21.6, -45.53) * mm, "end": v(-23.17, -51.37) * mm});
            skLineSegment(sketch, "E29.4.0.2", {"start": v(-18.4, -40.95) * mm, "end": v(-19.5, -45.02) * mm});
            skLineSegment(sketch, "E29.4.0.3", {"start": v(-11.54, -38.93) * mm, "end": v(-13.17, -45.02) * mm});
            skLineSegment(sketch, "E29.4.0.4", {"start": v(-14.55, -40.83) * mm, "end": v(-17.85, -40.83) * mm});
            skLineSegment(sketch, "E29.4.0.5", {"start": v(-15.5, -51.63) * mm, "end": v(-22.67, -51.63) * mm});
            skLineSegment(sketch, "E29.4.0.6", {"start": v(-13.5, -38.93) * mm, "end": v(-15.14, -45.02) * mm});
            skLineSegment(sketch, "E29.4.0.7", {"start": v(-16.93, -49.72) * mm, "end": v(-20.23, -49.72) * mm});
            skLineSegment(sketch, "E29.4.0.8", {"start": v(-15.48, -44.32) * mm, "end": v(-18.78, -44.32) * mm});
            skLineSegment(sketch, "E29.4.0.9", {"start": v(-15.28, -45.53) * mm, "end": v(-16.37, -49.61) * mm});
            skLineSegment(sketch, "E29.4.0.10", {"start": v(-13.3, -45.53) * mm, "end": v(-14.92, -51.54) * mm});
            skLineSegment(sketch, "E29.4.0.11", {"start": v(-21.47, -45.02) * mm, "end": v(-19.9, -39.17) * mm});
            skLineSegment(sketch, "E29.4.0.12", {"start": v(-19.45, -38.93) * mm, "end": v(-14.04, -38.93) * mm});
            skLineSegment(sketch, "E29.4.0.13", {"start": v(-19.9, -39.17) * mm, "end": v(-18.4, -40.95) * mm});
            skLineSegment(sketch, "E29.4.0.14", {"start": v(-19.5, -45.02) * mm, "end": v(-21.47, -45.02) * mm});
            skLineSegment(sketch, "E29.4.0.15", {"start": v(-20.68, -49.42) * mm, "end": v(-19.63, -45.53) * mm});
            skLineSegment(sketch, "E29.4.0.16", {"start": v(-17.85, -40.83) * mm, "end": v(-19.45, -38.93) * mm});
            skLineSegment(sketch, "E29.4.0.17", {"start": v(-22.67, -51.63) * mm, "end": v(-20.23, -49.72) * mm});
            skLineSegment(sketch, "E29.4.0.18", {"start": v(-13.5, -38.93) * mm, "end": v(-11.54, -38.93) * mm});
            skLineSegment(sketch, "E29.4.0.19", {"start": v(-19.63, -45.53) * mm, "end": v(-21.6, -45.53) * mm});
            skLineSegment(sketch, "E29.4.0.20", {"start": v(-23.17, -51.37) * mm, "end": v(-20.68, -49.42) * mm});
            skLineSegment(sketch, "E29.4.0.21", {"start": v(-15.5, -51.63) * mm, "end": v(-16.93, -49.72) * mm});
            skLineSegment(sketch, "E29.4.0.22", {"start": v(-14.04, -38.93) * mm, "end": v(-14.55, -40.83) * mm});
            skLineSegment(sketch, "E29.4.0.23", {"start": v(-16.37, -49.61) * mm, "end": v(-14.92, -51.54) * mm});
            skLineSegment(sketch, "E29.4.0.24", {"start": v(-18.78, -44.32) * mm, "end": v(-19.04, -45.28) * mm});
            skLineSegment(sketch, "E29.4.0.25", {"start": v(-15.28, -45.53) * mm, "end": v(-13.3, -45.53) * mm});
            skLineSegment(sketch, "E29.4.0.26", {"start": v(-15.14, -45.02) * mm, "end": v(-13.17, -45.02) * mm});
            skLineSegment(sketch, "E29.4.0.27", {"start": v(-16, -46.23) * mm, "end": v(-15.48, -44.32) * mm});
            skLineSegment(sketch, "E29.4.1.0", {"start": v(-19.3, -26.8) * mm, "end": v(-16, -26.8) * mm});
            skLineSegment(sketch, "E29.4.1.1", {"start": v(-21.6, -26.1) * mm, "end": v(-23.17, -31.94) * mm});
            skLineSegment(sketch, "E29.4.1.2", {"start": v(-18.4, -21.52) * mm, "end": v(-19.5, -25.6) * mm});
            skLineSegment(sketch, "E29.4.1.3", {"start": v(-11.54, -19.5) * mm, "end": v(-13.17, -25.6) * mm});
            skLineSegment(sketch, "E29.4.1.4", {"start": v(-14.55, -21.4) * mm, "end": v(-17.85, -21.4) * mm});
            skLineSegment(sketch, "E29.4.1.5", {"start": v(-15.5, -32.2) * mm, "end": v(-22.67, -32.2) * mm});
            skLineSegment(sketch, "E29.4.1.6", {"start": v(-13.5, -19.5) * mm, "end": v(-15.14, -25.6) * mm});
            skLineSegment(sketch, "E29.4.1.7", {"start": v(-16.93, -30.29) * mm, "end": v(-20.23, -30.29) * mm});
            skLineSegment(sketch, "E29.4.1.8", {"start": v(-15.48, -24.9) * mm, "end": v(-18.78, -24.9) * mm});
            skLineSegment(sketch, "E29.4.1.9", {"start": v(-15.28, -26.1) * mm, "end": v(-16.37, -30.18) * mm});
            skLineSegment(sketch, "E29.4.1.10", {"start": v(-13.3, -26.1) * mm, "end": v(-14.92, -32.11) * mm});
            skLineSegment(sketch, "E29.4.1.11", {"start": v(-21.47, -25.6) * mm, "end": v(-19.9, -19.74) * mm});
            skLineSegment(sketch, "E29.4.1.12", {"start": v(-19.45, -19.5) * mm, "end": v(-14.04, -19.5) * mm});
            skLineSegment(sketch, "E29.4.1.13", {"start": v(-19.9, -19.74) * mm, "end": v(-18.4, -21.52) * mm});
            skLineSegment(sketch, "E29.4.1.14", {"start": v(-19.5, -25.6) * mm, "end": v(-21.47, -25.6) * mm});
            skLineSegment(sketch, "E29.4.1.15", {"start": v(-20.68, -30) * mm, "end": v(-19.63, -26.1) * mm});
            skLineSegment(sketch, "E29.4.1.16", {"start": v(-17.85, -21.4) * mm, "end": v(-19.45, -19.5) * mm});
            skLineSegment(sketch, "E29.4.1.17", {"start": v(-22.67, -32.2) * mm, "end": v(-20.23, -30.29) * mm});
            skLineSegment(sketch, "E29.4.1.18", {"start": v(-13.5, -19.5) * mm, "end": v(-11.54, -19.5) * mm});
            skLineSegment(sketch, "E29.4.1.19", {"start": v(-19.63, -26.1) * mm, "end": v(-21.6, -26.1) * mm});
            skLineSegment(sketch, "E29.4.1.20", {"start": v(-23.17, -31.94) * mm, "end": v(-20.68, -30) * mm});
            skLineSegment(sketch, "E29.4.1.21", {"start": v(-15.5, -32.2) * mm, "end": v(-16.93, -30.29) * mm});
            skLineSegment(sketch, "E29.4.1.22", {"start": v(-14.04, -19.5) * mm, "end": v(-14.55, -21.4) * mm});
            skLineSegment(sketch, "E29.4.1.23", {"start": v(-16.37, -30.18) * mm, "end": v(-14.92, -32.11) * mm});
            skLineSegment(sketch, "E29.4.1.24", {"start": v(-18.78, -24.9) * mm, "end": v(-19.3, -26.8) * mm});
            skLineSegment(sketch, "E29.4.1.25", {"start": v(-15.28, -26.1) * mm, "end": v(-13.3, -26.1) * mm});
            skLineSegment(sketch, "E29.4.1.26", {"start": v(-15.14, -25.6) * mm, "end": v(-13.17, -25.6) * mm});
            skLineSegment(sketch, "E29.4.1.27", {"start": v(-16, -26.8) * mm, "end": v(-15.48, -24.9) * mm});
            skLineSegment(sketch, "E29.4.2.0", {"start": v(-19.3, -7.37) * mm, "end": v(-16, -7.37) * mm});
            skLineSegment(sketch, "E29.4.2.1", {"start": v(-21.6, -6.67) * mm, "end": v(-23.17, -12.51) * mm});
            skLineSegment(sketch, "E29.4.2.2", {"start": v(-18.4, -2.1) * mm, "end": v(-19.5, -6.16) * mm});
            skLineSegment(sketch, "E29.4.2.3", {"start": v(-11.54, -0.06) * mm, "end": v(-13.17, -6.16) * mm});
            skLineSegment(sketch, "E29.4.2.4", {"start": v(-14.55, -1.97) * mm, "end": v(-17.85, -1.97) * mm});
            skLineSegment(sketch, "E29.4.2.5", {"start": v(-15.5, -12.76) * mm, "end": v(-22.67, -12.76) * mm});
            skLineSegment(sketch, "E29.4.2.6", {"start": v(-13.5, -0.06) * mm, "end": v(-15.14, -6.16) * mm});
            skLineSegment(sketch, "E29.4.2.7", {"start": v(-16.93, -10.86) * mm, "end": v(-20.23, -10.86) * mm});
            skLineSegment(sketch, "E29.4.2.8", {"start": v(-15.48, -5.46) * mm, "end": v(-18.78, -5.46) * mm});
            skLineSegment(sketch, "E29.4.2.9", {"start": v(-15.28, -6.67) * mm, "end": v(-16.37, -10.75) * mm});
            skLineSegment(sketch, "E29.4.2.10", {"start": v(-13.3, -6.67) * mm, "end": v(-14.92, -12.68) * mm});
            skLineSegment(sketch, "E29.4.2.11", {"start": v(-21.47, -6.16) * mm, "end": v(-19.9, -0.31) * mm});
            skLineSegment(sketch, "E29.4.2.12", {"start": v(-19.45, -0.06) * mm, "end": v(-14.04, -0.06) * mm});
            skLineSegment(sketch, "E29.4.2.13", {"start": v(-19.9, -0.31) * mm, "end": v(-18.4, -2.1) * mm});
            skLineSegment(sketch, "E29.4.2.14", {"start": v(-19.5, -6.16) * mm, "end": v(-21.47, -6.16) * mm});
            skLineSegment(sketch, "E29.4.2.15", {"start": v(-20.68, -10.56) * mm, "end": v(-19.63, -6.67) * mm});
            skLineSegment(sketch, "E29.4.2.16", {"start": v(-17.85, -1.97) * mm, "end": v(-19.45, -0.06) * mm});
            skLineSegment(sketch, "E29.4.2.17", {"start": v(-22.67, -12.76) * mm, "end": v(-20.23, -10.86) * mm});
            skLineSegment(sketch, "E29.4.2.18", {"start": v(-13.5, -0.06) * mm, "end": v(-11.54, -0.06) * mm});
            skLineSegment(sketch, "E29.4.2.19", {"start": v(-19.63, -6.67) * mm, "end": v(-21.6, -6.67) * mm});
            skLineSegment(sketch, "E29.4.2.20", {"start": v(-23.17, -12.51) * mm, "end": v(-20.68, -10.56) * mm});
            skLineSegment(sketch, "E29.4.2.21", {"start": v(-15.5, -12.76) * mm, "end": v(-16.93, -10.86) * mm});
            skLineSegment(sketch, "E29.4.2.22", {"start": v(-14.04, -0.06) * mm, "end": v(-14.55, -1.97) * mm});
            skLineSegment(sketch, "E29.4.2.23", {"start": v(-16.37, -10.75) * mm, "end": v(-14.92, -12.68) * mm});
            skLineSegment(sketch, "E29.4.2.24", {"start": v(-18.78, -5.46) * mm, "end": v(-19.3, -7.37) * mm});
            skLineSegment(sketch, "E29.4.2.25", {"start": v(-15.28, -6.67) * mm, "end": v(-13.3, -6.67) * mm});
            skLineSegment(sketch, "E29.4.2.26", {"start": v(-15.14, -6.16) * mm, "end": v(-13.17, -6.16) * mm});
            skLineSegment(sketch, "E29.4.2.27", {"start": v(-16, -7.37) * mm, "end": v(-15.48, -5.46) * mm});
            skLineSegment(sketch, "E29.direction1", {"start": v(17.39, -51.37) * mm, "end": v(7.25, -51.37) * mm, "construction": true});
            skLineSegment(sketch, "E29.direction2", {"start": v(17.39, -51.37) * mm, "end": v(17.39, -31.94) * mm, "construction": true});
            skLineSegment(sketch, "E30.direction1", {"start": v(7.75, -12.76) * mm, "end": v(33.15, -12.76) * mm, "construction": true});
            skLineSegment(sketch, "E30.direction2", {"start": v(7.75, -12.76) * mm, "end": v(7.75, 6.29) * mm, "construction": true});
            skLineSegment(sketch, "E31.0.0.1", {"start": v(26.01, 17.08) * mm, "end": v(22.7, 17.08) * mm});
            skLineSegment(sketch, "E31.3.0.1", {"start": v(21.26, 11.68) * mm, "end": v(24.56, 11.68) * mm});
            skLineSegment(sketch, "E31.6.0.1", {"start": v(15.87, 17.08) * mm, "end": v(12.57, 17.08) * mm});
            skLineSegment(sketch, "E31.9.0.1", {"start": v(10.97, 18.99) * mm, "end": v(16.38, 18.99) * mm});
            skLineSegment(sketch, "E31.12.0.1", {"start": v(25.08, 13.59) * mm, "end": v(21.77, 13.59) * mm});
            skLineSegment(sketch, "E31.15.0.1", {"start": v(27.05, 18.99) * mm, "end": v(25.41, 12.9) * mm});
            skLineSegment(sketch, "E31.18.0.1", {"start": v(17.39, 6.54) * mm, "end": v(19.88, 8.49) * mm});
            skLineSegment(sketch, "E31.21.0.1", {"start": v(22.15, 16.96) * mm, "end": v(21.06, 12.9) * mm});
            skLineSegment(sketch, "E31.24.0.1", {"start": v(25.28, 12.38) * mm, "end": v(27.25, 12.38) * mm});
            skLineSegment(sketch, "E31.27.0.1", {"start": v(24.18, 8.3) * mm, "end": v(25.64, 6.37) * mm});
            skLineSegment(sketch, "E31.30.0.1", {"start": v(17.89, 6.29) * mm, "end": v(20.33, 8.2) * mm});
            skLineSegment(sketch, "E31.33.0.1", {"start": v(17.11, 12.38) * mm, "end": v(15.5, 6.37) * mm});
            skLineSegment(sketch, "E31.36.0.1", {"start": v(12.57, 17.08) * mm, "end": v(10.97, 18.99) * mm});
            skLineSegment(sketch, "E31.39.0.1", {"start": v(27.05, 18.99) * mm, "end": v(29.02, 18.99) * mm});
            skLineSegment(sketch, "E31.42.0.1", {"start": v(19.88, 8.49) * mm, "end": v(20.92, 12.38) * mm});
            skLineSegment(sketch, "E31.45.0.1", {"start": v(29.02, 18.99) * mm, "end": v(27.39, 12.9) * mm});
            skLineSegment(sketch, "E31.48.0.1", {"start": v(23.63, 8.2) * mm, "end": v(20.33, 8.2) * mm});
            skLineSegment(sketch, "E31.51.0.1", {"start": v(16.9, 18.99) * mm, "end": v(15.27, 12.9) * mm});
            skLineSegment(sketch, "E31.54.0.1", {"start": v(25.41, 12.9) * mm, "end": v(27.39, 12.9) * mm});
            skLineSegment(sketch, "E31.57.0.1", {"start": v(25.06, 6.29) * mm, "end": v(17.89, 6.29) * mm});
            skLineSegment(sketch, "E31.60.0.1", {"start": v(9.74, 8.49) * mm, "end": v(10.78, 12.38) * mm});
            skLineSegment(sketch, "E31.63.0.1", {"start": v(8.95, 12.9) * mm, "end": v(10.52, 18.74) * mm});
            skLineSegment(sketch, "E31.66.0.1", {"start": v(21.11, 18.99) * mm, "end": v(26.52, 18.99) * mm});
            skLineSegment(sketch, "E31.69.0.1", {"start": v(27.25, 12.38) * mm, "end": v(25.64, 6.37) * mm});
            skLineSegment(sketch, "E31.72.0.1", {"start": v(25.28, 12.38) * mm, "end": v(24.18, 8.3) * mm});
            skLineSegment(sketch, "E31.75.0.1", {"start": v(13.49, 8.2) * mm, "end": v(10.19, 8.2) * mm});
            skLineSegment(sketch, "E31.78.0.1", {"start": v(14.04, 8.3) * mm, "end": v(15.5, 6.37) * mm});
            skLineSegment(sketch, "E31.81.0.1", {"start": v(25.06, 6.29) * mm, "end": v(23.63, 8.2) * mm});
            skLineSegment(sketch, "E31.84.0.1", {"start": v(12.01, 16.96) * mm, "end": v(10.92, 12.9) * mm});
            skLineSegment(sketch, "E31.87.0.1", {"start": v(18.95, 12.38) * mm, "end": v(17.39, 6.54) * mm});
            skLineSegment(sketch, "E31.90.0.1", {"start": v(11.12, 11.68) * mm, "end": v(14.43, 11.68) * mm});
            skLineSegment(sketch, "E31.93.0.1", {"start": v(14.93, 6.29) * mm, "end": v(13.49, 8.2) * mm});
            skLineSegment(sketch, "E31.96.0.1", {"start": v(14.93, 6.29) * mm, "end": v(7.75, 6.29) * mm});
            skLineSegment(sketch, "E31.99.0.1", {"start": v(15.14, 12.38) * mm, "end": v(14.04, 8.3) * mm});
            skLineSegment(sketch, "E31.102.0.1", {"start": v(19.09, 12.9) * mm, "end": v(20.65, 18.74) * mm});
            skLineSegment(sketch, "E31.105.0.1", {"start": v(14.94, 13.59) * mm, "end": v(11.63, 13.59) * mm});
            skLineSegment(sketch, "E31.108.0.1", {"start": v(20.65, 18.74) * mm, "end": v(22.15, 16.96) * mm});
            skLineSegment(sketch, "E31.111.0.1", {"start": v(18.88, 18.99) * mm, "end": v(17.25, 12.9) * mm});
            skLineSegment(sketch, "E31.114.0.1", {"start": v(10.52, 18.74) * mm, "end": v(12.01, 16.96) * mm});
            skLineSegment(sketch, "E31.117.0.1", {"start": v(10.92, 12.9) * mm, "end": v(8.95, 12.9) * mm});
            skLineSegment(sketch, "E31.120.0.1", {"start": v(7.75, 6.29) * mm, "end": v(10.19, 8.2) * mm});
            skLineSegment(sketch, "E31.123.0.1", {"start": v(15.14, 12.38) * mm, "end": v(17.11, 12.38) * mm});
            skLineSegment(sketch, "E31.126.0.1", {"start": v(11.63, 13.59) * mm, "end": v(11.12, 11.68) * mm});
            skLineSegment(sketch, "E31.129.0.1", {"start": v(16.38, 18.99) * mm, "end": v(15.87, 17.08) * mm});
            skLineSegment(sketch, "E31.132.0.1", {"start": v(21.77, 13.59) * mm, "end": v(21.26, 11.68) * mm});
            skLineSegment(sketch, "E31.135.0.1", {"start": v(14.43, 11.68) * mm, "end": v(14.94, 13.59) * mm});
            skLineSegment(sketch, "E31.138.0.1", {"start": v(21.06, 12.9) * mm, "end": v(19.09, 12.9) * mm});
            skLineSegment(sketch, "E31.141.0.1", {"start": v(26.52, 18.99) * mm, "end": v(26.01, 17.08) * mm});
            skLineSegment(sketch, "E31.144.0.1", {"start": v(15.27, 12.9) * mm, "end": v(17.25, 12.9) * mm});
            skLineSegment(sketch, "E31.147.0.1", {"start": v(20.92, 12.38) * mm, "end": v(18.95, 12.38) * mm});
            skLineSegment(sketch, "E31.150.0.1", {"start": v(16.9, 18.99) * mm, "end": v(18.88, 18.99) * mm});
            skLineSegment(sketch, "E31.153.0.1", {"start": v(24.56, 11.68) * mm, "end": v(25.08, 13.59) * mm});
            skLineSegment(sketch, "E31.156.0.1", {"start": v(22.7, 17.08) * mm, "end": v(21.11, 18.99) * mm});
            skLineSegment(sketch, "E31.159.0.1", {"start": v(10.78, 12.38) * mm, "end": v(8.81, 12.38) * mm});
            skLineSegment(sketch, "E31.162.0.1", {"start": v(7.25, 6.54) * mm, "end": v(9.74, 8.49) * mm});
            skLineSegment(sketch, "E31.165.0.1", {"start": v(8.81, 12.38) * mm, "end": v(7.25, 6.54) * mm});
            skLineSegment(sketch, "E32.0.1.0", {"start": v(27.05, 43.12) * mm, "end": v(25.41, 37.02) * mm});
            skLineSegment(sketch, "E32.0.1.1", {"start": v(25.08, 37.72) * mm, "end": v(21.77, 37.72) * mm});
            skLineSegment(sketch, "E32.0.1.2", {"start": v(26.01, 41.21) * mm, "end": v(22.7, 41.21) * mm});
            skLineSegment(sketch, "E32.0.1.3", {"start": v(22.15, 41.09) * mm, "end": v(21.06, 37.02) * mm});
            skLineSegment(sketch, "E32.0.1.4", {"start": v(8.81, 36.51) * mm, "end": v(7.25, 30.67) * mm});
            skLineSegment(sketch, "E32.0.1.5", {"start": v(18.95, 36.51) * mm, "end": v(17.39, 30.67) * mm});
            skLineSegment(sketch, "E32.0.1.6", {"start": v(8.95, 37.02) * mm, "end": v(10.52, 42.87) * mm});
            skLineSegment(sketch, "E32.0.1.7", {"start": v(25.28, 36.51) * mm, "end": v(24.18, 32.43) * mm});
            skLineSegment(sketch, "E32.0.1.8", {"start": v(17.11, 36.51) * mm, "end": v(15.5, 30.5) * mm});
            skLineSegment(sketch, "E32.0.1.9", {"start": v(27.25, 36.51) * mm, "end": v(25.64, 30.5) * mm});
            skLineSegment(sketch, "E32.0.1.10", {"start": v(15.14, 36.51) * mm, "end": v(14.04, 32.43) * mm});
            skLineSegment(sketch, "E32.0.1.11", {"start": v(18.88, 43.12) * mm, "end": v(17.25, 37.02) * mm});
            skLineSegment(sketch, "E32.0.1.12", {"start": v(12.01, 41.09) * mm, "end": v(10.92, 37.02) * mm});
            skLineSegment(sketch, "E32.0.1.13", {"start": v(13.49, 32.32) * mm, "end": v(10.19, 32.32) * mm});
            skLineSegment(sketch, "E32.0.1.14", {"start": v(21.11, 43.12) * mm, "end": v(26.52, 43.12) * mm});
            skLineSegment(sketch, "E32.0.1.15", {"start": v(21.26, 35.81) * mm, "end": v(24.56, 35.81) * mm});
            skLineSegment(sketch, "E32.0.1.16", {"start": v(19.09, 37.02) * mm, "end": v(20.65, 42.87) * mm});
            skLineSegment(sketch, "E32.0.1.17", {"start": v(29.02, 43.12) * mm, "end": v(27.39, 37.02) * mm});
            skLineSegment(sketch, "E32.0.1.18", {"start": v(10.97, 43.12) * mm, "end": v(16.38, 43.12) * mm});
            skLineSegment(sketch, "E32.0.1.19", {"start": v(25.06, 30.42) * mm, "end": v(17.89, 30.42) * mm});
            skLineSegment(sketch, "E32.0.1.20", {"start": v(14.93, 30.42) * mm, "end": v(7.75, 30.42) * mm});
            skLineSegment(sketch, "E32.0.1.21", {"start": v(23.63, 32.32) * mm, "end": v(20.33, 32.32) * mm});
            skLineSegment(sketch, "E32.0.1.22", {"start": v(16.9, 43.12) * mm, "end": v(15.27, 37.02) * mm});
            skLineSegment(sketch, "E32.0.1.23", {"start": v(22.7, 41.21) * mm, "end": v(21.11, 43.12) * mm});
            skLineSegment(sketch, "E32.0.1.24", {"start": v(21.06, 37.02) * mm, "end": v(19.09, 37.02) * mm});
            skLineSegment(sketch, "E32.0.1.25", {"start": v(7.25, 30.67) * mm, "end": v(9.74, 32.62) * mm});
            skLineSegment(sketch, "E32.0.1.26", {"start": v(17.89, 30.42) * mm, "end": v(20.33, 32.32) * mm});
            skLineSegment(sketch, "E32.0.1.27", {"start": v(25.41, 37.02) * mm, "end": v(27.39, 37.02) * mm});
            skLineSegment(sketch, "E32.0.1.28", {"start": v(26.52, 43.12) * mm, "end": v(26.01, 41.21) * mm});
            skLineSegment(sketch, "E32.0.1.29", {"start": v(10.52, 42.87) * mm, "end": v(12.01, 41.09) * mm});
            skLineSegment(sketch, "E32.0.1.30", {"start": v(9.74, 32.62) * mm, "end": v(10.78, 36.51) * mm});
            skLineSegment(sketch, "E32.0.1.31", {"start": v(16.9, 43.12) * mm, "end": v(18.88, 43.12) * mm});
            skLineSegment(sketch, "E32.0.1.32", {"start": v(20.65, 42.87) * mm, "end": v(22.15, 41.09) * mm});
            skLineSegment(sketch, "E32.0.1.33", {"start": v(7.75, 30.42) * mm, "end": v(10.19, 32.32) * mm});
            skLineSegment(sketch, "E32.0.1.34", {"start": v(10.92, 37.02) * mm, "end": v(8.95, 37.02) * mm});
            skLineSegment(sketch, "E32.0.1.35", {"start": v(15.87, 41.21) * mm, "end": v(12.57, 41.21) * mm});
            skLineSegment(sketch, "E32.0.1.36", {"start": v(12.57, 41.21) * mm, "end": v(10.97, 43.12) * mm});
            skLineSegment(sketch, "E32.0.1.37", {"start": v(15.27, 37.02) * mm, "end": v(17.25, 37.02) * mm});
            skLineSegment(sketch, "E32.0.1.38", {"start": v(14.04, 32.43) * mm, "end": v(15.5, 30.5) * mm});
            skLineSegment(sketch, "E32.0.1.39", {"start": v(25.06, 30.42) * mm, "end": v(23.63, 32.32) * mm});
            skLineSegment(sketch, "E32.0.1.40", {"start": v(11.12, 35.81) * mm, "end": v(14.43, 35.81) * mm});
            skLineSegment(sketch, "E32.0.1.41", {"start": v(25.28, 36.51) * mm, "end": v(27.25, 36.51) * mm});
            skLineSegment(sketch, "E32.0.1.42", {"start": v(10.78, 36.51) * mm, "end": v(8.81, 36.51) * mm});
            skLineSegment(sketch, "E32.0.1.43", {"start": v(16.38, 43.12) * mm, "end": v(15.87, 41.21) * mm});
            skLineSegment(sketch, "E32.0.1.44", {"start": v(15.14, 36.51) * mm, "end": v(17.11, 36.51) * mm});
            skLineSegment(sketch, "E32.0.1.45", {"start": v(14.93, 30.42) * mm, "end": v(13.49, 32.32) * mm});
            skLineSegment(sketch, "E32.0.1.46", {"start": v(24.18, 32.43) * mm, "end": v(25.64, 30.5) * mm});
            skLineSegment(sketch, "E32.0.1.47", {"start": v(27.05, 43.12) * mm, "end": v(29.02, 43.12) * mm});
            skLineSegment(sketch, "E32.0.1.48", {"start": v(17.39, 30.67) * mm, "end": v(19.88, 32.62) * mm});
            skLineSegment(sketch, "E32.0.1.49", {"start": v(19.88, 32.62) * mm, "end": v(20.92, 36.51) * mm});
            skLineSegment(sketch, "E32.0.1.50", {"start": v(20.92, 36.51) * mm, "end": v(18.95, 36.51) * mm});
            skLineSegment(sketch, "E32.0.1.51", {"start": v(14.94, 37.72) * mm, "end": v(11.63, 37.72) * mm});
            skLineSegment(sketch, "E32.0.1.52", {"start": v(24.56, 35.81) * mm, "end": v(25.08, 37.72) * mm});
            skLineSegment(sketch, "E32.0.1.53", {"start": v(21.77, 37.72) * mm, "end": v(21.26, 35.81) * mm});
            skLineSegment(sketch, "E32.0.1.54", {"start": v(11.63, 37.72) * mm, "end": v(11.12, 35.81) * mm});
            skLineSegment(sketch, "E32.0.1.55", {"start": v(14.43, 35.81) * mm, "end": v(14.94, 37.72) * mm});
            skLineSegment(sketch, "E32.direction1", {"start": v(7.25, 6.54) * mm, "end": v(32.65, 6.54) * mm, "construction": true});
            skLineSegment(sketch, "E32.direction2", {"start": v(7.25, 6.54) * mm, "end": v(7.25, 30.67) * mm, "construction": true});
            skLineSegment(sketch, "E33.1.0.0", {"start": v(-8.82, 12.38) * mm, "end": v(-10.43, 6.37) * mm});
            skLineSegment(sketch, "E33.1.0.1", {"start": v(-17.19, 18.99) * mm, "end": v(-18.82, 12.9) * mm});
            skLineSegment(sketch, "E33.1.0.2", {"start": v(-17.12, 12.38) * mm, "end": v(-18.68, 6.54) * mm});
            skLineSegment(sketch, "E33.1.0.3", {"start": v(-27.26, 12.38) * mm, "end": v(-28.82, 6.54) * mm});
            skLineSegment(sketch, "E33.1.0.4", {"start": v(-25.1, 18.99) * mm, "end": v(-19.69, 18.99) * mm});
            skLineSegment(sketch, "E33.1.0.5", {"start": v(-14.96, 18.99) * mm, "end": v(-9.55, 18.99) * mm});
            skLineSegment(sketch, "E33.1.0.6", {"start": v(-16.98, 12.9) * mm, "end": v(-15.41, 18.74) * mm});
            skLineSegment(sketch, "E33.1.0.7", {"start": v(-27.12, 12.9) * mm, "end": v(-25.55, 18.74) * mm});
            skLineSegment(sketch, "E33.1.0.8", {"start": v(-21.14, 6.29) * mm, "end": v(-28.32, 6.29) * mm});
            skLineSegment(sketch, "E33.1.0.9", {"start": v(-11, 6.29) * mm, "end": v(-18.18, 6.29) * mm});
            skLineSegment(sketch, "E33.1.0.10", {"start": v(-7.05, 18.99) * mm, "end": v(-8.68, 12.9) * mm});
            skLineSegment(sketch, "E33.1.0.11", {"start": v(-18.96, 12.38) * mm, "end": v(-20.57, 6.37) * mm});
            skLineSegment(sketch, "E33.1.0.12", {"start": v(-9.02, 18.99) * mm, "end": v(-10.65, 12.9) * mm});
            skLineSegment(sketch, "E33.1.0.13", {"start": v(-14.8, 11.68) * mm, "end": v(-11.5, 11.68) * mm});
            skLineSegment(sketch, "E33.1.0.14", {"start": v(-20.2, 17.08) * mm, "end": v(-23.5, 17.08) * mm});
            skLineSegment(sketch, "E33.1.0.15", {"start": v(-24.94, 11.68) * mm, "end": v(-21.64, 11.68) * mm});
            skLineSegment(sketch, "E33.1.0.16", {"start": v(-12.44, 8.2) * mm, "end": v(-15.74, 8.2) * mm});
            skLineSegment(sketch, "E33.1.0.17", {"start": v(-13.92, 16.96) * mm, "end": v(-15, 12.9) * mm});
            skLineSegment(sketch, "E33.1.0.18", {"start": v(-16.19, 8.49) * mm, "end": v(-15.14, 12.38) * mm});
            skLineSegment(sketch, "E33.1.0.19", {"start": v(-19.16, 18.99) * mm, "end": v(-20.8, 12.9) * mm});
            skLineSegment(sketch, "E33.1.0.20", {"start": v(-25.28, 12.38) * mm, "end": v(-27.26, 12.38) * mm});
            skLineSegment(sketch, "E33.1.0.21", {"start": v(-25.55, 18.74) * mm, "end": v(-24.06, 16.96) * mm});
            skLineSegment(sketch, "E33.1.0.22", {"start": v(-28.82, 6.54) * mm, "end": v(-26.33, 8.49) * mm});
            skLineSegment(sketch, "E33.1.0.23", {"start": v(-10.65, 12.9) * mm, "end": v(-8.68, 12.9) * mm});
            skLineSegment(sketch, "E33.1.0.24", {"start": v(-10.06, 17.08) * mm, "end": v(-13.36, 17.08) * mm});
            skLineSegment(sketch, "E33.1.0.25", {"start": v(-18.18, 6.29) * mm, "end": v(-15.74, 8.2) * mm});
            skLineSegment(sketch, "E33.1.0.26", {"start": v(-20.93, 12.38) * mm, "end": v(-22.02, 8.3) * mm});
            skLineSegment(sketch, "E33.1.0.27", {"start": v(-10.8, 12.38) * mm, "end": v(-8.82, 12.38) * mm});
            skLineSegment(sketch, "E33.1.0.28", {"start": v(-10.8, 12.38) * mm, "end": v(-11.88, 8.3) * mm});
            skLineSegment(sketch, "E33.1.0.29", {"start": v(-9.02, 18.99) * mm, "end": v(-7.05, 18.99) * mm});
            skLineSegment(sketch, "E33.1.0.30", {"start": v(-9.55, 18.99) * mm, "end": v(-10.06, 17.08) * mm});
            skLineSegment(sketch, "E33.1.0.31", {"start": v(-24.06, 16.96) * mm, "end": v(-25.15, 12.9) * mm});
            skLineSegment(sketch, "E33.1.0.32", {"start": v(-20.8, 12.9) * mm, "end": v(-18.82, 12.9) * mm});
            skLineSegment(sketch, "E33.1.0.33", {"start": v(-11.88, 8.3) * mm, "end": v(-10.43, 6.37) * mm});
            skLineSegment(sketch, "E33.1.0.34", {"start": v(-28.32, 6.29) * mm, "end": v(-25.88, 8.2) * mm});
            skLineSegment(sketch, "E33.1.0.35", {"start": v(-22.02, 8.3) * mm, "end": v(-20.57, 6.37) * mm});
            skLineSegment(sketch, "E33.1.0.36", {"start": v(-21.14, 6.29) * mm, "end": v(-22.58, 8.2) * mm});
            skLineSegment(sketch, "E33.1.0.37", {"start": v(-13.36, 17.08) * mm, "end": v(-14.96, 18.99) * mm});
            skLineSegment(sketch, "E33.1.0.38", {"start": v(-11, 13.59) * mm, "end": v(-14.3, 13.59) * mm});
            skLineSegment(sketch, "E33.1.0.39", {"start": v(-22.58, 8.2) * mm, "end": v(-25.88, 8.2) * mm});
            skLineSegment(sketch, "E33.1.0.40", {"start": v(-21.13, 13.59) * mm, "end": v(-24.43, 13.59) * mm});
            skLineSegment(sketch, "E33.1.0.41", {"start": v(-26.33, 8.49) * mm, "end": v(-25.28, 12.38) * mm});
            skLineSegment(sketch, "E33.1.0.42", {"start": v(-15.41, 18.74) * mm, "end": v(-13.92, 16.96) * mm});
            skLineSegment(sketch, "E33.1.0.43", {"start": v(-11, 6.29) * mm, "end": v(-12.44, 8.2) * mm});
            skLineSegment(sketch, "E33.1.0.44", {"start": v(-18.68, 6.54) * mm, "end": v(-16.19, 8.49) * mm});
            skLineSegment(sketch, "E33.1.0.45", {"start": v(-23.5, 17.08) * mm, "end": v(-25.1, 18.99) * mm});
            skLineSegment(sketch, "E33.1.0.46", {"start": v(-21.64, 11.68) * mm, "end": v(-21.13, 13.59) * mm});
            skLineSegment(sketch, "E33.1.0.47", {"start": v(-11.5, 11.68) * mm, "end": v(-11, 13.59) * mm});
            skLineSegment(sketch, "E33.1.0.48", {"start": v(-24.43, 13.59) * mm, "end": v(-24.94, 11.68) * mm});
            skLineSegment(sketch, "E33.1.0.49", {"start": v(-20.93, 12.38) * mm, "end": v(-18.96, 12.38) * mm});
            skLineSegment(sketch, "E33.1.0.50", {"start": v(-15, 12.9) * mm, "end": v(-16.98, 12.9) * mm});
            skLineSegment(sketch, "E33.1.0.51", {"start": v(-15.14, 12.38) * mm, "end": v(-17.12, 12.38) * mm});
            skLineSegment(sketch, "E33.1.0.52", {"start": v(-25.15, 12.9) * mm, "end": v(-27.12, 12.9) * mm});
            skLineSegment(sketch, "E33.1.0.53", {"start": v(-14.3, 13.59) * mm, "end": v(-14.8, 11.68) * mm});
            skLineSegment(sketch, "E33.1.0.54", {"start": v(-19.69, 18.99) * mm, "end": v(-20.2, 17.08) * mm});
            skLineSegment(sketch, "E33.1.0.55", {"start": v(-19.16, 18.99) * mm, "end": v(-17.19, 18.99) * mm});
            skLineSegment(sketch, "E33.direction1", {"start": v(7.25, 6.54) * mm, "end": v(-28.82, 6.54) * mm, "construction": true});
            skLineSegment(sketch, "E34.bottom", {"start": v(-23.17, -33.34) * mm, "end": v(25.64, -33.34) * mm});
            skLineSegment(sketch, "E34.top", {"start": v(-23.17, -35.24) * mm, "end": v(25.64, -35.24) * mm});
            skLineSegment(sketch, "E34.left", {"start": v(-23.17, -33.34) * mm, "end": v(-23.17, -35.24) * mm});
            skLineSegment(sketch, "E34.right", {"start": v(25.64, -33.34) * mm, "end": v(25.64, -35.24) * mm});
            skLineSegment(sketch, "E35.bottom", {"start": v(-23.17, -13.9) * mm, "end": v(25.64, -13.9) * mm});
            skLineSegment(sketch, "E35.top", {"start": v(-23.17, -15.81) * mm, "end": v(25.64, -15.81) * mm});
            skLineSegment(sketch, "E35.left", {"start": v(-23.17, -13.9) * mm, "end": v(-23.17, -15.81) * mm});
            skLineSegment(sketch, "E35.right", {"start": v(25.64, -13.9) * mm, "end": v(25.64, -15.81) * mm});
            skLineSegment(sketch, "E36.bottom", {"start": v(-29.27, -44.32) * mm, "end": v(-25.84, -44.32) * mm});
            skLineSegment(sketch, "E36.top", {"start": v(-29.27, -46.23) * mm, "end": v(-22.42, -46.23) * mm});
            skLineSegment(sketch, "E36.left", {"start": v(-29.27, -44.32) * mm, "end": v(-29.27, -46.23) * mm});
            skLineSegment(sketch, "E36.right", {"start": v(-22.42, -44.32) * mm, "end": v(-22.42, -45.28) * mm});
            skLineSegment(sketch, "E37.bottom", {"start": v(-26.8, -41.21) * mm, "end": v(-24.9, -41.21) * mm});
            skLineSegment(sketch, "E37.top", {"start": v(-26.8, -43.82) * mm, "end": v(-25.84, -43.82) * mm});
            skLineSegment(sketch, "E37.left", {"start": v(-26.8, -41.21) * mm, "end": v(-26.8, -43.82) * mm});
            skLineSegment(sketch, "E37.right", {"start": v(-24.9, -41.21) * mm, "end": v(-24.9, -43.82) * mm});
            skLineSegment(sketch, "E38.bottom", {"start": v(-26.8, -46.74) * mm, "end": v(-24.9, -46.74) * mm});
            skLineSegment(sketch, "E38.top", {"start": v(-26.8, -49.34) * mm, "end": v(-24.9, -49.34) * mm});
            skLineSegment(sketch, "E38.left", {"start": v(-26.8, -46.74) * mm, "end": v(-26.8, -49.34) * mm});
            skLineSegment(sketch, "E38.right", {"start": v(-24.9, -46.74) * mm, "end": v(-24.9, -49.34) * mm});
            skLineSegment(sketch, "E39", {"start": v(-19.04, -45.28) * mm, "end": v(-19.3, -46.23) * mm});
            skLineSegment(sketch, "E40", {"start": v(-22.42, -45.28) * mm, "end": v(-22.42, -46.23) * mm});
            skLineSegment(sketch, "E41", {"start": v(-25.84, -43.82) * mm, "end": v(-24.9, -43.82) * mm});
            skLineSegment(sketch, "E42", {"start": v(-25.84, -44.32) * mm, "end": v(-22.42, -44.32) * mm});
            skLineSegment(sketch, "E43.bottom", {"start": v(-23.17, 5.14) * mm, "end": v(25.64, 5.14) * mm});
            skLineSegment(sketch, "E43.top", {"start": v(-23.17, 3.24) * mm, "end": v(25.64, 3.24) * mm});
            skLineSegment(sketch, "E43.left", {"start": v(-23.17, 5.14) * mm, "end": v(-23.17, 3.24) * mm});
            skLineSegment(sketch, "E43.right", {"start": v(25.64, 5.14) * mm, "end": v(25.64, 3.24) * mm});
            skLineSegment(sketch, "E44.bottom", {"start": v(29.43, 27.11) * mm, "end": v(6.57, 27.11) * mm});
            skLineSegment(sketch, "E44.top", {"start": v(29.43, 20.51) * mm, "end": v(6.57, 20.51) * mm});
            skLineSegment(sketch, "E44.left", {"start": v(29.43, 27.11) * mm, "end": v(29.43, 20.51) * mm});
            skLineSegment(sketch, "E44.right", {"start": v(6.57, 27.11) * mm, "end": v(6.57, 20.51) * mm});
            skPoint(sketch, "E45.firstSnap0", {"position": v(29.43, 23.81) * mm});
            skLineSegment(sketch, "E45.bottom", {"start": v(29.43, 51.24) * mm, "end": v(6.57, 51.24) * mm});
            skLineSegment(sketch, "E45.top", {"start": v(29.43, 44.64) * mm, "end": v(6.57, 44.64) * mm});
            skLineSegment(sketch, "E45.left", {"start": v(29.43, 51.24) * mm, "end": v(29.43, 44.64) * mm});
            skLineSegment(sketch, "E45.right", {"start": v(6.57, 51.24) * mm, "end": v(6.57, 44.64) * mm});
            skLineSegment(sketch, "E46.bottom", {"start": v(-6.64, 27.11) * mm, "end": v(-29.5, 27.11) * mm});
            skLineSegment(sketch, "E46.top", {"start": v(-6.64, 20.51) * mm, "end": v(-29.5, 20.51) * mm});
            skLineSegment(sketch, "E46.left", {"start": v(-6.64, 27.11) * mm, "end": v(-6.64, 20.51) * mm});
            skLineSegment(sketch, "E46.right", {"start": v(-29.5, 27.11) * mm, "end": v(-29.5, 20.51) * mm});
            skLineSegment(sketch, "E47.bottom", {"start": v(-6.64, 51.24) * mm, "end": v(-29.5, 51.24) * mm});
            skLineSegment(sketch, "E47.top", {"start": v(-6.64, 30.42) * mm, "end": v(-29.5, 30.42) * mm});
            skLineSegment(sketch, "E47.left", {"start": v(-6.64, 51.24) * mm, "end": v(-6.64, 30.42) * mm});
            skLineSegment(sketch, "E47.right", {"start": v(-29.5, 51.24) * mm, "end": v(-29.5, 30.42) * mm});
            skLineSegment(sketch, "E48.0.1.0", {"start": v(-25.84, -24.9) * mm, "end": v(-22.42, -24.9) * mm});
            skLineSegment(sketch, "E48.0.1.1", {"start": v(-29.27, -24.9) * mm, "end": v(-25.84, -24.9) * mm});
            skLineSegment(sketch, "E48.0.1.2", {"start": v(-26.8, -21.78) * mm, "end": v(-26.8, -24.38) * mm});
            skLineSegment(sketch, "E48.0.1.3", {"start": v(-26.8, -21.78) * mm, "end": v(-24.9, -21.78) * mm});
            skLineSegment(sketch, "E48.0.1.4", {"start": v(-24.9, -21.78) * mm, "end": v(-24.9, -24.38) * mm});
            skLineSegment(sketch, "E48.0.1.5", {"start": v(-24.9, -27.3) * mm, "end": v(-24.9, -29.9) * mm});
            skLineSegment(sketch, "E48.0.1.6", {"start": v(-26.8, -29.9) * mm, "end": v(-24.9, -29.9) * mm});
            skLineSegment(sketch, "E48.0.1.7", {"start": v(-26.8, -27.3) * mm, "end": v(-26.8, -29.9) * mm});
            skLineSegment(sketch, "E48.0.1.8", {"start": v(-26.8, -27.3) * mm, "end": v(-24.9, -27.3) * mm});
            skLineSegment(sketch, "E48.0.1.9", {"start": v(-29.27, -24.9) * mm, "end": v(-29.27, -26.8) * mm});
            skLineSegment(sketch, "E48.0.1.10", {"start": v(-29.27, -26.8) * mm, "end": v(-22.42, -26.8) * mm});
            skLineSegment(sketch, "E48.0.1.11", {"start": v(-26.8, -24.38) * mm, "end": v(-25.84, -24.38) * mm});
            skLineSegment(sketch, "E48.0.1.12", {"start": v(-22.42, -24.9) * mm, "end": v(-22.42, -25.84) * mm});
            skLineSegment(sketch, "E48.0.1.13", {"start": v(-22.42, -25.84) * mm, "end": v(-22.42, -26.8) * mm});
            skLineSegment(sketch, "E48.0.1.14", {"start": v(-25.84, -24.38) * mm, "end": v(-24.9, -24.38) * mm});
            skLineSegment(sketch, "E48.0.2.0", {"start": v(-25.84, -5.46) * mm, "end": v(-22.42, -5.46) * mm});
            skLineSegment(sketch, "E48.0.2.1", {"start": v(-29.27, -5.46) * mm, "end": v(-25.84, -5.46) * mm});
            skLineSegment(sketch, "E48.0.2.2", {"start": v(-26.8, -2.35) * mm, "end": v(-26.8, -4.95) * mm});
            skLineSegment(sketch, "E48.0.2.3", {"start": v(-26.8, -2.35) * mm, "end": v(-24.9, -2.35) * mm});
            skLineSegment(sketch, "E48.0.2.4", {"start": v(-24.9, -2.35) * mm, "end": v(-24.9, -4.95) * mm});
            skLineSegment(sketch, "E48.0.2.5", {"start": v(-24.9, -7.87) * mm, "end": v(-24.9, -10.48) * mm});
            skLineSegment(sketch, "E48.0.2.6", {"start": v(-26.8, -10.48) * mm, "end": v(-24.9, -10.48) * mm});
            skLineSegment(sketch, "E48.0.2.7", {"start": v(-26.8, -7.87) * mm, "end": v(-26.8, -10.48) * mm});
            skLineSegment(sketch, "E48.0.2.8", {"start": v(-26.8, -7.87) * mm, "end": v(-24.9, -7.87) * mm});
            skLineSegment(sketch, "E48.0.2.9", {"start": v(-29.27, -5.46) * mm, "end": v(-29.27, -7.37) * mm});
            skLineSegment(sketch, "E48.0.2.10", {"start": v(-29.27, -7.37) * mm, "end": v(-22.42, -7.37) * mm});
            skLineSegment(sketch, "E48.0.2.11", {"start": v(-26.8, -4.95) * mm, "end": v(-25.84, -4.95) * mm});
            skLineSegment(sketch, "E48.0.2.12", {"start": v(-22.42, -5.46) * mm, "end": v(-22.42, -6.41) * mm});
            skLineSegment(sketch, "E48.0.2.13", {"start": v(-22.42, -6.41) * mm, "end": v(-22.42, -7.37) * mm});
            skLineSegment(sketch, "E48.0.2.14", {"start": v(-25.84, -4.95) * mm, "end": v(-24.9, -4.95) * mm});
            skLineSegment(sketch, "E48.direction1", {"start": v(-26.8, -49.34) * mm, "end": v(-1.4, -49.34) * mm, "construction": true});
            skLineSegment(sketch, "E48.direction2", {"start": v(-26.8, -49.34) * mm, "end": v(-26.8, -29.9) * mm, "construction": true});
            skSolve(sketch);
        }
        {
            var Q0;
            Q0 = qSketchRegion(id + "F2", true);
            extrude(context, id + "F3", {"entities" : qUnion([Q0]), "operationType" : NewBodyOperationType.REMOVE, "endBound" : BoundingType.THROUGH_ALL, "oppositeDirection" : true, "depth" : 25.4 * mm});
        }
        {
            var Q0;
            Q0=makeQuery(id+"F1.opExtrude","SWEPT_EDGE",EDGE,{"disambiguationData":[OSD([sQuery(id+"F0.wireOp",EDGE,"E0.top"),sQuery(id+"F0.wireOp",EDGE,"E0.right")])]});
            var Q1;
            Q1=makeQuery(id+"F1.opExtrude","SWEPT_EDGE",EDGE,{"disambiguationData":[OSD([sQuery(id+"F0.wireOp",EDGE,"E0.top"),sQuery(id+"F0.wireOp",EDGE,"E0.left")])]});
            var Q2;
            Q2=makeQuery(id+"F1.opExtrude","SWEPT_EDGE",EDGE,{"disambiguationData":[OSD([sQuery(id+"F0.wireOp",EDGE,"E0.bottom"),sQuery(id+"F0.wireOp",EDGE,"E0.left")])]});
            var Q3;
            Q3=makeQuery(id+"F1.opExtrude","SWEPT_EDGE",EDGE,{"disambiguationData":[OSD([sQuery(id+"F0.wireOp",EDGE,"E0.bottom"),sQuery(id+"F0.wireOp",EDGE,"E0.right")])]});
            fillet(context, id + "F4", {"entities" : qUnion([Q0, Q1, Q2, Q3]), "radius" : 2.54 * mm, "tangentPropagation" : true, "allowEdgeOverflow" : false});
        }
    });
